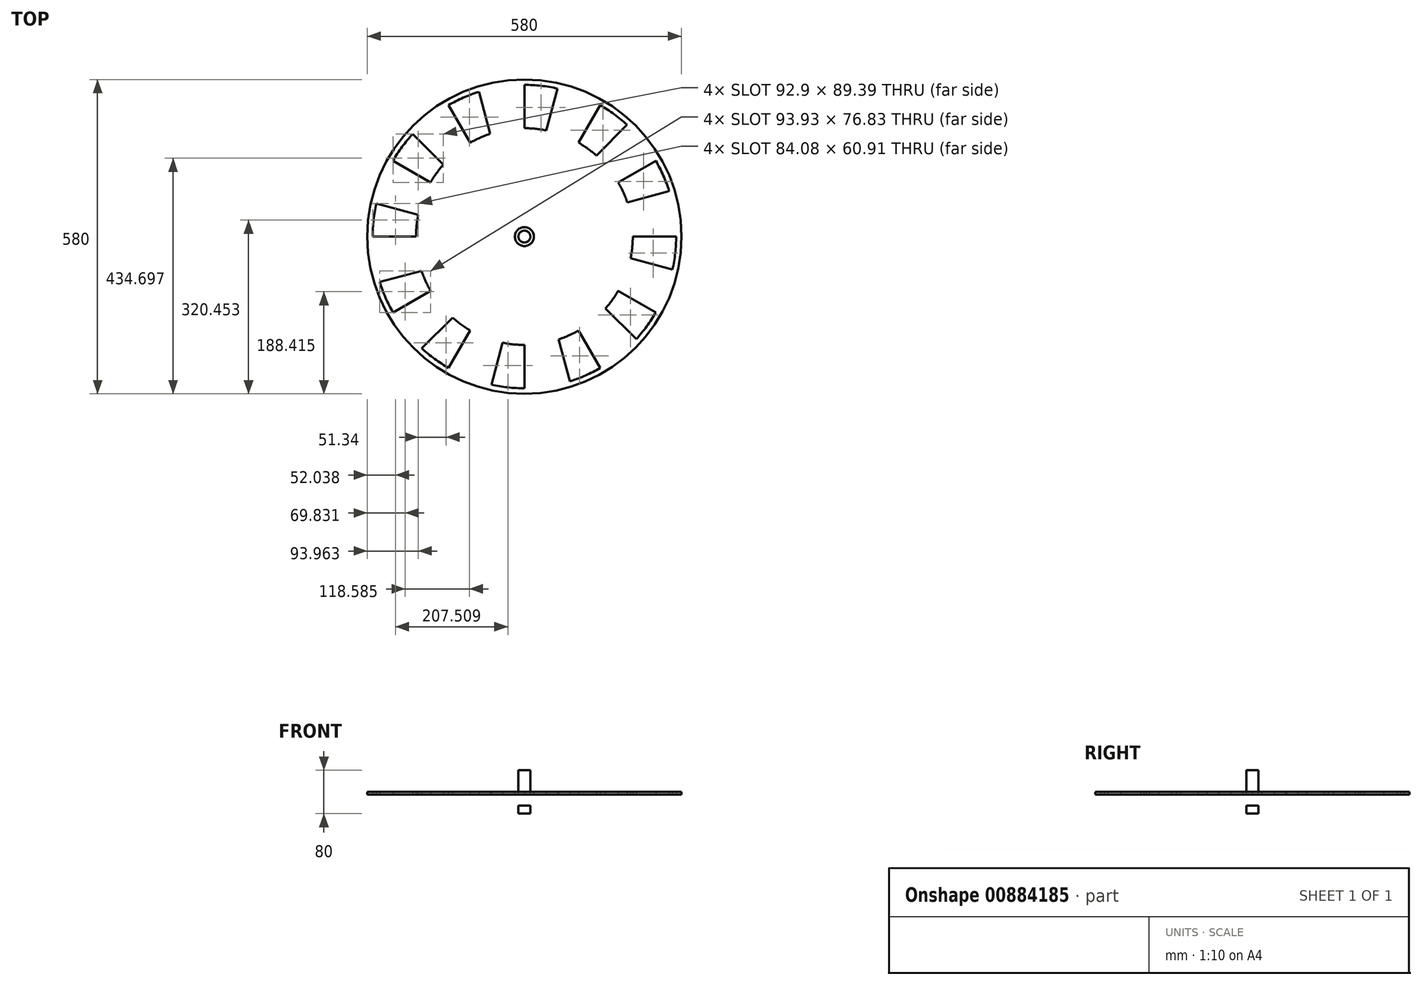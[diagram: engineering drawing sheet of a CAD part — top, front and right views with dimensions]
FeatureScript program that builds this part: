
annotation { "Feature Type Name" : "Feature", "Feature Type Description" : "" }
export const myFeature = defineFeature(function(context is Context, id is Id, definition is map)
    precondition{}
    {
        {
            var Q0;
            Q0=qCreatedBy(makeId("Top.planeOp"),FACE);
            var sketch = newSketch(context, id + "F0", { "sketchPlane" : qUnion([Q0])});
            skArc(sketch, "E0", {"start": v(9.54, 136.41) * mm, "mid": v(4.77, 136.66) * mm, "end": v(0, 136.75) * mm});
            skArc(sketch, "E1", {"start": v(8, 114.55) * mm, "mid": v(4, 114.76) * mm, "end": v(0, 114.83) * mm});
            skLineSegment(sketch, "E2", {"start": v(0, 0) * mm, "end": v(0, 38.61) * mm, "construction": true});
            skLineSegment(sketch, "E3", {"start": v(0, 10) * mm, "end": v(0, 0) * mm, "construction": true});
            skLineSegment(sketch, "E4", {"start": v(0, 0) * mm, "end": v(-47.77, 0) * mm, "construction": true});
            skLineSegment(sketch, "E5", {"start": v(0, 114.83) * mm, "end": v(0, 136.75) * mm});
            skLineSegment(sketch, "E6", {"start": v(8, 114.55) * mm, "end": v(9.54, 136.41) * mm});
            skArc(sketch, "E7.1.0", {"start": v(-10, 114.4) * mm, "mid": v(-14, 113.98) * mm, "end": v(-17.96, 113.42) * mm});
            skLineSegment(sketch, "E7.1.1", {"start": v(-17.96, 113.42) * mm, "end": v(-21.4, 135.06) * mm});
            skArc(sketch, "E7.1.2", {"start": v(-11.92, 136.23) * mm, "mid": v(-16.67, 135.73) * mm, "end": v(-21.4, 135.06) * mm});
            skLineSegment(sketch, "E7.1.3", {"start": v(-10, 114.4) * mm, "end": v(-11.92, 136.23) * mm});
            skArc(sketch, "E7.2.0", {"start": v(-27.78, 111.42) * mm, "mid": v(-31.65, 110.39) * mm, "end": v(-35.49, 109.21) * mm});
            skLineSegment(sketch, "E7.2.1", {"start": v(-35.49, 109.21) * mm, "end": v(-42.26, 130.05) * mm});
            skArc(sketch, "E7.2.2", {"start": v(-33.08, 132.68) * mm, "mid": v(-37.7, 131.45) * mm, "end": v(-42.26, 130.05) * mm});
            skLineSegment(sketch, "E7.2.3", {"start": v(-27.78, 111.42) * mm, "end": v(-33.08, 132.68) * mm});
            skArc(sketch, "E7.3.0", {"start": v(-44.87, 105.7) * mm, "mid": v(-48.53, 104.07) * mm, "end": v(-52.13, 102.32) * mm});
            skLineSegment(sketch, "E7.3.1", {"start": v(-52.13, 102.32) * mm, "end": v(-62.08, 121.84) * mm});
            skArc(sketch, "E7.3.2", {"start": v(-53.43, 125.88) * mm, "mid": v(-57.8, 123.93) * mm, "end": v(-62.08, 121.84) * mm});
            skLineSegment(sketch, "E7.3.3", {"start": v(-44.87, 105.7) * mm, "end": v(-53.43, 125.88) * mm});
            skArc(sketch, "E7.4.0", {"start": v(-60.85, 97.38) * mm, "mid": v(-64.21, 95.2) * mm, "end": v(-67.5, 92.9) * mm});
            skLineSegment(sketch, "E7.4.1", {"start": v(-67.5, 92.9) * mm, "end": v(-80.38, 110.63) * mm});
            skArc(sketch, "E7.4.2", {"start": v(-72.47, 115.97) * mm, "mid": v(-76.47, 113.37) * mm, "end": v(-80.38, 110.63) * mm});
            skLineSegment(sketch, "E7.4.3", {"start": v(-60.85, 97.38) * mm, "end": v(-72.47, 115.97) * mm});
            skArc(sketch, "E7.5.0", {"start": v(-75.34, 86.67) * mm, "mid": v(-78.32, 83.98) * mm, "end": v(-81.2, 81.2) * mm});
            skLineSegment(sketch, "E7.5.1", {"start": v(-81.2, 81.2) * mm, "end": v(-96.7, 96.7) * mm});
            skArc(sketch, "E7.5.2", {"start": v(-89.71, 103.2) * mm, "mid": v(-93.26, 100.01) * mm, "end": v(-96.7, 96.7) * mm});
            skLineSegment(sketch, "E7.5.3", {"start": v(-75.34, 86.67) * mm, "end": v(-89.71, 103.2) * mm});
            skArc(sketch, "E7.6.0", {"start": v(-87.97, 73.81) * mm, "mid": v(-90.5, 70.7) * mm, "end": v(-92.9, 67.5) * mm});
            skLineSegment(sketch, "E7.6.1", {"start": v(-92.9, 67.5) * mm, "end": v(-110.63, 80.38) * mm});
            skArc(sketch, "E7.6.2", {"start": v(-104.75, 87.9) * mm, "mid": v(-107.76, 84.19) * mm, "end": v(-110.63, 80.38) * mm});
            skLineSegment(sketch, "E7.6.3", {"start": v(-87.97, 73.81) * mm, "end": v(-104.75, 87.9) * mm});
            skArc(sketch, "E7.7.0", {"start": v(-98.43, 59.14) * mm, "mid": v(-100.44, 55.67) * mm, "end": v(-102.32, 52.13) * mm});
            skLineSegment(sketch, "E7.7.1", {"start": v(-102.32, 52.13) * mm, "end": v(-121.84, 62.08) * mm});
            skArc(sketch, "E7.7.2", {"start": v(-117.22, 70.43) * mm, "mid": v(-119.6, 66.3) * mm, "end": v(-121.84, 62.08) * mm});
            skLineSegment(sketch, "E7.7.3", {"start": v(-98.43, 59.14) * mm, "end": v(-117.22, 70.43) * mm});
            skArc(sketch, "E7.8.0", {"start": v(-106.47, 43.02) * mm, "mid": v(-107.9, 39.28) * mm, "end": v(-109.21, 35.49) * mm});
            skLineSegment(sketch, "E7.8.1", {"start": v(-109.21, 35.49) * mm, "end": v(-130.05, 42.26) * mm});
            skArc(sketch, "E7.8.2", {"start": v(-126.79, 51.23) * mm, "mid": v(-128.5, 46.77) * mm, "end": v(-130.05, 42.26) * mm});
            skLineSegment(sketch, "E7.8.3", {"start": v(-106.47, 43.02) * mm, "end": v(-126.79, 51.23) * mm});
            skArc(sketch, "E7.9.0", {"start": v(-111.9, 25.83) * mm, "mid": v(-112.72, 21.91) * mm, "end": v(-113.42, 17.96) * mm});
            skLineSegment(sketch, "E7.9.1", {"start": v(-113.42, 17.96) * mm, "end": v(-135.06, 21.4) * mm});
            skArc(sketch, "E7.9.2", {"start": v(-133.24, 30.76) * mm, "mid": v(-134.23, 26.1) * mm, "end": v(-135.06, 21.4) * mm});
            skLineSegment(sketch, "E7.9.3", {"start": v(-111.9, 25.83) * mm, "end": v(-133.24, 30.76) * mm});
            skArc(sketch, "E7.10.0", {"start": v(-114.55, 8) * mm, "mid": v(-114.76, 4) * mm, "end": v(-114.83, 0) * mm});
            skLineSegment(sketch, "E7.10.1", {"start": v(-114.83, 0) * mm, "end": v(-136.75, 0) * mm});
            skArc(sketch, "E7.10.2", {"start": v(-136.41, 9.54) * mm, "mid": v(-136.66, 4.77) * mm, "end": v(-136.75, 0) * mm});
            skLineSegment(sketch, "E7.10.3", {"start": v(-114.55, 8) * mm, "end": v(-136.41, 9.54) * mm});
            skArc(sketch, "E7.11.0", {"start": v(-114.4, -10) * mm, "mid": v(-113.98, -14) * mm, "end": v(-113.42, -17.96) * mm});
            skLineSegment(sketch, "E7.11.1", {"start": v(-113.42, -17.96) * mm, "end": v(-135.06, -21.4) * mm});
            skArc(sketch, "E7.11.2", {"start": v(-136.23, -11.92) * mm, "mid": v(-135.73, -16.67) * mm, "end": v(-135.06, -21.4) * mm});
            skLineSegment(sketch, "E7.11.3", {"start": v(-114.4, -10) * mm, "end": v(-136.23, -11.92) * mm});
            skArc(sketch, "E7.12.0", {"start": v(-111.42, -27.78) * mm, "mid": v(-110.39, -31.65) * mm, "end": v(-109.21, -35.49) * mm});
            skLineSegment(sketch, "E7.12.1", {"start": v(-109.21, -35.49) * mm, "end": v(-130.05, -42.26) * mm});
            skArc(sketch, "E7.12.2", {"start": v(-132.68, -33.08) * mm, "mid": v(-131.45, -37.7) * mm, "end": v(-130.05, -42.26) * mm});
            skLineSegment(sketch, "E7.12.3", {"start": v(-111.42, -27.78) * mm, "end": v(-132.68, -33.08) * mm});
            skArc(sketch, "E7.13.0", {"start": v(-105.7, -44.87) * mm, "mid": v(-104.07, -48.53) * mm, "end": v(-102.32, -52.13) * mm});
            skLineSegment(sketch, "E7.13.1", {"start": v(-102.32, -52.13) * mm, "end": v(-121.84, -62.08) * mm});
            skArc(sketch, "E7.13.2", {"start": v(-125.88, -53.43) * mm, "mid": v(-123.93, -57.8) * mm, "end": v(-121.84, -62.08) * mm});
            skLineSegment(sketch, "E7.13.3", {"start": v(-105.7, -44.87) * mm, "end": v(-125.88, -53.43) * mm});
            skArc(sketch, "E7.14.0", {"start": v(-97.38, -60.85) * mm, "mid": v(-95.2, -64.21) * mm, "end": v(-92.9, -67.5) * mm});
            skLineSegment(sketch, "E7.14.1", {"start": v(-92.9, -67.5) * mm, "end": v(-110.63, -80.38) * mm});
            skArc(sketch, "E7.14.2", {"start": v(-115.97, -72.47) * mm, "mid": v(-113.37, -76.47) * mm, "end": v(-110.63, -80.38) * mm});
            skLineSegment(sketch, "E7.14.3", {"start": v(-97.38, -60.85) * mm, "end": v(-115.97, -72.47) * mm});
            skArc(sketch, "E7.15.0", {"start": v(-86.67, -75.34) * mm, "mid": v(-83.98, -78.32) * mm, "end": v(-81.2, -81.2) * mm});
            skLineSegment(sketch, "E7.15.1", {"start": v(-81.2, -81.2) * mm, "end": v(-96.7, -96.7) * mm});
            skArc(sketch, "E7.15.2", {"start": v(-103.2, -89.71) * mm, "mid": v(-100.01, -93.26) * mm, "end": v(-96.7, -96.7) * mm});
            skLineSegment(sketch, "E7.15.3", {"start": v(-86.67, -75.34) * mm, "end": v(-103.2, -89.71) * mm});
            skArc(sketch, "E7.16.0", {"start": v(-73.81, -87.97) * mm, "mid": v(-70.7, -90.5) * mm, "end": v(-67.5, -92.9) * mm});
            skLineSegment(sketch, "E7.16.1", {"start": v(-67.5, -92.9) * mm, "end": v(-80.38, -110.63) * mm});
            skArc(sketch, "E7.16.2", {"start": v(-87.9, -104.75) * mm, "mid": v(-84.19, -107.76) * mm, "end": v(-80.38, -110.63) * mm});
            skLineSegment(sketch, "E7.16.3", {"start": v(-73.81, -87.97) * mm, "end": v(-87.9, -104.75) * mm});
            skArc(sketch, "E7.17.0", {"start": v(-59.14, -98.43) * mm, "mid": v(-55.67, -100.44) * mm, "end": v(-52.13, -102.32) * mm});
            skLineSegment(sketch, "E7.17.1", {"start": v(-52.13, -102.32) * mm, "end": v(-62.08, -121.84) * mm});
            skArc(sketch, "E7.17.2", {"start": v(-70.43, -117.22) * mm, "mid": v(-66.3, -119.6) * mm, "end": v(-62.08, -121.84) * mm});
            skLineSegment(sketch, "E7.17.3", {"start": v(-59.14, -98.43) * mm, "end": v(-70.43, -117.22) * mm});
            skArc(sketch, "E7.18.0", {"start": v(-43.02, -106.47) * mm, "mid": v(-39.28, -107.9) * mm, "end": v(-35.49, -109.21) * mm});
            skLineSegment(sketch, "E7.18.1", {"start": v(-35.49, -109.21) * mm, "end": v(-42.26, -130.05) * mm});
            skArc(sketch, "E7.18.2", {"start": v(-51.23, -126.79) * mm, "mid": v(-46.77, -128.5) * mm, "end": v(-42.26, -130.05) * mm});
            skLineSegment(sketch, "E7.18.3", {"start": v(-43.02, -106.47) * mm, "end": v(-51.23, -126.79) * mm});
            skArc(sketch, "E7.19.0", {"start": v(-25.83, -111.9) * mm, "mid": v(-21.91, -112.72) * mm, "end": v(-17.96, -113.42) * mm});
            skLineSegment(sketch, "E7.19.1", {"start": v(-17.96, -113.42) * mm, "end": v(-21.4, -135.06) * mm});
            skArc(sketch, "E7.19.2", {"start": v(-30.76, -133.24) * mm, "mid": v(-26.1, -134.23) * mm, "end": v(-21.4, -135.06) * mm});
            skLineSegment(sketch, "E7.19.3", {"start": v(-25.83, -111.9) * mm, "end": v(-30.76, -133.24) * mm});
            skArc(sketch, "E7.20.0", {"start": v(-8, -114.55) * mm, "mid": v(-4, -114.76) * mm, "end": v(0, -114.83) * mm});
            skLineSegment(sketch, "E7.20.1", {"start": v(0, -114.83) * mm, "end": v(0, -136.75) * mm});
            skArc(sketch, "E7.20.2", {"start": v(-9.54, -136.41) * mm, "mid": v(-4.77, -136.66) * mm, "end": v(0, -136.75) * mm});
            skLineSegment(sketch, "E7.20.3", {"start": v(-8, -114.55) * mm, "end": v(-9.54, -136.41) * mm});
            skArc(sketch, "E7.21.0", {"start": v(10, -114.4) * mm, "mid": v(14, -113.98) * mm, "end": v(17.96, -113.42) * mm});
            skLineSegment(sketch, "E7.21.1", {"start": v(17.96, -113.42) * mm, "end": v(21.4, -135.06) * mm});
            skArc(sketch, "E7.21.2", {"start": v(11.92, -136.23) * mm, "mid": v(16.67, -135.73) * mm, "end": v(21.4, -135.06) * mm});
            skLineSegment(sketch, "E7.21.3", {"start": v(10, -114.4) * mm, "end": v(11.92, -136.23) * mm});
            skArc(sketch, "E7.22.0", {"start": v(27.78, -111.42) * mm, "mid": v(31.65, -110.39) * mm, "end": v(35.49, -109.21) * mm});
            skLineSegment(sketch, "E7.22.1", {"start": v(35.49, -109.21) * mm, "end": v(42.26, -130.05) * mm});
            skArc(sketch, "E7.22.2", {"start": v(33.08, -132.68) * mm, "mid": v(37.7, -131.45) * mm, "end": v(42.26, -130.05) * mm});
            skLineSegment(sketch, "E7.22.3", {"start": v(27.78, -111.42) * mm, "end": v(33.08, -132.68) * mm});
            skArc(sketch, "E7.23.0", {"start": v(44.87, -105.7) * mm, "mid": v(48.53, -104.07) * mm, "end": v(52.13, -102.32) * mm});
            skLineSegment(sketch, "E7.23.1", {"start": v(52.13, -102.32) * mm, "end": v(62.08, -121.84) * mm});
            skArc(sketch, "E7.23.2", {"start": v(53.43, -125.88) * mm, "mid": v(57.8, -123.93) * mm, "end": v(62.08, -121.84) * mm});
            skLineSegment(sketch, "E7.23.3", {"start": v(44.87, -105.7) * mm, "end": v(53.43, -125.88) * mm});
            skArc(sketch, "E7.24.0", {"start": v(60.85, -97.38) * mm, "mid": v(64.21, -95.2) * mm, "end": v(67.5, -92.9) * mm});
            skLineSegment(sketch, "E7.24.1", {"start": v(67.5, -92.9) * mm, "end": v(80.38, -110.63) * mm});
            skArc(sketch, "E7.24.2", {"start": v(72.47, -115.97) * mm, "mid": v(76.47, -113.37) * mm, "end": v(80.38, -110.63) * mm});
            skLineSegment(sketch, "E7.24.3", {"start": v(60.85, -97.38) * mm, "end": v(72.47, -115.97) * mm});
            skArc(sketch, "E7.25.0", {"start": v(75.34, -86.67) * mm, "mid": v(78.32, -83.98) * mm, "end": v(81.2, -81.2) * mm});
            skLineSegment(sketch, "E7.25.1", {"start": v(81.2, -81.2) * mm, "end": v(96.7, -96.7) * mm});
            skArc(sketch, "E7.25.2", {"start": v(89.71, -103.2) * mm, "mid": v(93.26, -100.01) * mm, "end": v(96.7, -96.7) * mm});
            skLineSegment(sketch, "E7.25.3", {"start": v(75.34, -86.67) * mm, "end": v(89.71, -103.2) * mm});
            skArc(sketch, "E7.26.0", {"start": v(87.97, -73.81) * mm, "mid": v(90.5, -70.7) * mm, "end": v(92.9, -67.5) * mm});
            skLineSegment(sketch, "E7.26.1", {"start": v(92.9, -67.5) * mm, "end": v(110.63, -80.38) * mm});
            skArc(sketch, "E7.26.2", {"start": v(104.75, -87.9) * mm, "mid": v(107.76, -84.19) * mm, "end": v(110.63, -80.38) * mm});
            skLineSegment(sketch, "E7.26.3", {"start": v(87.97, -73.81) * mm, "end": v(104.75, -87.9) * mm});
            skArc(sketch, "E7.27.0", {"start": v(98.43, -59.14) * mm, "mid": v(100.44, -55.67) * mm, "end": v(102.32, -52.13) * mm});
            skLineSegment(sketch, "E7.27.1", {"start": v(102.32, -52.13) * mm, "end": v(121.84, -62.08) * mm});
            skArc(sketch, "E7.27.2", {"start": v(117.22, -70.43) * mm, "mid": v(119.6, -66.3) * mm, "end": v(121.84, -62.08) * mm});
            skLineSegment(sketch, "E7.27.3", {"start": v(98.43, -59.14) * mm, "end": v(117.22, -70.43) * mm});
            skArc(sketch, "E7.28.0", {"start": v(106.47, -43.02) * mm, "mid": v(107.9, -39.28) * mm, "end": v(109.21, -35.49) * mm});
            skLineSegment(sketch, "E7.28.1", {"start": v(109.21, -35.49) * mm, "end": v(130.05, -42.26) * mm});
            skArc(sketch, "E7.28.2", {"start": v(126.79, -51.23) * mm, "mid": v(128.5, -46.77) * mm, "end": v(130.05, -42.26) * mm});
            skLineSegment(sketch, "E7.28.3", {"start": v(106.47, -43.02) * mm, "end": v(126.79, -51.23) * mm});
            skArc(sketch, "E7.29.0", {"start": v(111.9, -25.83) * mm, "mid": v(112.72, -21.91) * mm, "end": v(113.42, -17.96) * mm});
            skLineSegment(sketch, "E7.29.1", {"start": v(113.42, -17.96) * mm, "end": v(135.06, -21.4) * mm});
            skArc(sketch, "E7.29.2", {"start": v(133.24, -30.76) * mm, "mid": v(134.23, -26.1) * mm, "end": v(135.06, -21.4) * mm});
            skLineSegment(sketch, "E7.29.3", {"start": v(111.9, -25.83) * mm, "end": v(133.24, -30.76) * mm});
            skArc(sketch, "E7.30.0", {"start": v(114.55, -8) * mm, "mid": v(114.76, -4) * mm, "end": v(114.83, 0) * mm});
            skLineSegment(sketch, "E7.30.1", {"start": v(114.83, 0) * mm, "end": v(136.75, 0) * mm});
            skArc(sketch, "E7.30.2", {"start": v(136.41, -9.54) * mm, "mid": v(136.66, -4.77) * mm, "end": v(136.75, 0) * mm});
            skLineSegment(sketch, "E7.30.3", {"start": v(114.55, -8) * mm, "end": v(136.41, -9.54) * mm});
            skArc(sketch, "E7.31.0", {"start": v(114.4, 10) * mm, "mid": v(113.98, 14) * mm, "end": v(113.42, 17.96) * mm});
            skLineSegment(sketch, "E7.31.1", {"start": v(113.42, 17.96) * mm, "end": v(135.06, 21.4) * mm});
            skArc(sketch, "E7.31.2", {"start": v(136.23, 11.92) * mm, "mid": v(135.73, 16.67) * mm, "end": v(135.06, 21.4) * mm});
            skLineSegment(sketch, "E7.31.3", {"start": v(114.4, 10) * mm, "end": v(136.23, 11.92) * mm});
            skArc(sketch, "E7.32.0", {"start": v(111.42, 27.78) * mm, "mid": v(110.39, 31.65) * mm, "end": v(109.21, 35.49) * mm});
            skLineSegment(sketch, "E7.32.1", {"start": v(109.21, 35.49) * mm, "end": v(130.05, 42.26) * mm});
            skArc(sketch, "E7.32.2", {"start": v(132.68, 33.08) * mm, "mid": v(131.45, 37.7) * mm, "end": v(130.05, 42.26) * mm});
            skLineSegment(sketch, "E7.32.3", {"start": v(111.42, 27.78) * mm, "end": v(132.68, 33.08) * mm});
            skArc(sketch, "E7.33.0", {"start": v(105.7, 44.87) * mm, "mid": v(104.07, 48.53) * mm, "end": v(102.32, 52.13) * mm});
            skLineSegment(sketch, "E7.33.1", {"start": v(102.32, 52.13) * mm, "end": v(121.84, 62.08) * mm});
            skArc(sketch, "E7.33.2", {"start": v(125.88, 53.43) * mm, "mid": v(123.93, 57.8) * mm, "end": v(121.84, 62.08) * mm});
            skLineSegment(sketch, "E7.33.3", {"start": v(105.7, 44.87) * mm, "end": v(125.88, 53.43) * mm});
            skArc(sketch, "E7.34.0", {"start": v(97.38, 60.85) * mm, "mid": v(95.2, 64.21) * mm, "end": v(92.9, 67.5) * mm});
            skLineSegment(sketch, "E7.34.1", {"start": v(92.9, 67.5) * mm, "end": v(110.63, 80.38) * mm});
            skArc(sketch, "E7.34.2", {"start": v(115.97, 72.47) * mm, "mid": v(113.37, 76.47) * mm, "end": v(110.63, 80.38) * mm});
            skLineSegment(sketch, "E7.34.3", {"start": v(97.38, 60.85) * mm, "end": v(115.97, 72.47) * mm});
            skArc(sketch, "E7.35.0", {"start": v(86.67, 75.34) * mm, "mid": v(83.98, 78.32) * mm, "end": v(81.2, 81.2) * mm});
            skLineSegment(sketch, "E7.35.1", {"start": v(81.2, 81.2) * mm, "end": v(96.7, 96.7) * mm});
            skArc(sketch, "E7.35.2", {"start": v(103.2, 89.71) * mm, "mid": v(100.01, 93.26) * mm, "end": v(96.7, 96.7) * mm});
            skLineSegment(sketch, "E7.35.3", {"start": v(86.67, 75.34) * mm, "end": v(103.2, 89.71) * mm});
            skArc(sketch, "E7.36.0", {"start": v(73.81, 87.97) * mm, "mid": v(70.7, 90.5) * mm, "end": v(67.5, 92.9) * mm});
            skLineSegment(sketch, "E7.36.1", {"start": v(67.5, 92.9) * mm, "end": v(80.38, 110.63) * mm});
            skArc(sketch, "E7.36.2", {"start": v(87.9, 104.75) * mm, "mid": v(84.19, 107.76) * mm, "end": v(80.38, 110.63) * mm});
            skLineSegment(sketch, "E7.36.3", {"start": v(73.81, 87.97) * mm, "end": v(87.9, 104.75) * mm});
            skArc(sketch, "E7.37.0", {"start": v(59.14, 98.43) * mm, "mid": v(55.67, 100.44) * mm, "end": v(52.13, 102.32) * mm});
            skLineSegment(sketch, "E7.37.1", {"start": v(52.13, 102.32) * mm, "end": v(62.08, 121.84) * mm});
            skArc(sketch, "E7.37.2", {"start": v(70.43, 117.22) * mm, "mid": v(66.3, 119.6) * mm, "end": v(62.08, 121.84) * mm});
            skLineSegment(sketch, "E7.37.3", {"start": v(59.14, 98.43) * mm, "end": v(70.43, 117.22) * mm});
            skArc(sketch, "E7.38.0", {"start": v(43.02, 106.47) * mm, "mid": v(39.28, 107.9) * mm, "end": v(35.49, 109.21) * mm});
            skLineSegment(sketch, "E7.38.1", {"start": v(35.49, 109.21) * mm, "end": v(42.26, 130.05) * mm});
            skArc(sketch, "E7.38.2", {"start": v(51.23, 126.79) * mm, "mid": v(46.77, 128.5) * mm, "end": v(42.26, 130.05) * mm});
            skLineSegment(sketch, "E7.38.3", {"start": v(43.02, 106.47) * mm, "end": v(51.23, 126.79) * mm});
            skArc(sketch, "E7.39.0", {"start": v(25.83, 111.9) * mm, "mid": v(21.91, 112.72) * mm, "end": v(17.96, 113.42) * mm});
            skLineSegment(sketch, "E7.39.1", {"start": v(17.96, 113.42) * mm, "end": v(21.4, 135.06) * mm});
            skArc(sketch, "E7.39.2", {"start": v(30.76, 133.24) * mm, "mid": v(26.1, 134.23) * mm, "end": v(21.4, 135.06) * mm});
            skLineSegment(sketch, "E7.39.3", {"start": v(25.83, 111.9) * mm, "end": v(30.76, 133.24) * mm});
            skCircle(sketch, "E8", {"center": v(0, 0) * mm, "radius": 290 * mm});
            skArc(sketch, "E9", {"start": v(40.17, 195.92) * mm, "mid": v(20.2, 198.98) * mm, "end": v(0, 200) * mm});
            skArc(sketch, "E10", {"start": v(60.9, 273.3) * mm, "mid": v(30.64, 278.32) * mm, "end": v(0, 280) * mm});
            skLineSegment(sketch, "E11", {"start": v(0, 0) * mm, "end": v(0, 38.61) * mm});
            skLineSegment(sketch, "E12.trimOffspring", {"start": v(0, 200) * mm, "end": v(0, 280) * mm});
            skLineSegment(sketch, "E13.trimOffspring", {"start": v(40.17, 195.92) * mm, "end": v(60.9, 273.3) * mm});
            skLineSegment(sketch, "E14.trimOffspring", {"start": v(0, 114.83) * mm, "end": v(0, 145) * mm});
            skArc(sketch, "E15.1.0", {"start": v(-63.17, 189.76) * mm, "mid": v(-82, 182.42) * mm, "end": v(-100, 173.2) * mm});
            skLineSegment(sketch, "E15.1.1", {"start": v(-100, 173.2) * mm, "end": v(-140, 242.49) * mm});
            skArc(sketch, "E15.1.2", {"start": v(-83.9, 267.13) * mm, "mid": v(-112.63, 256.35) * mm, "end": v(-140, 242.49) * mm});
            skLineSegment(sketch, "E15.1.3", {"start": v(-63.17, 189.76) * mm, "end": v(-83.9, 267.13) * mm});
            skArc(sketch, "E15.2.0", {"start": v(-149.59, 132.75) * mm, "mid": v(-162.23, 116.97) * mm, "end": v(-173.2, 100) * mm});
            skLineSegment(sketch, "E15.2.1", {"start": v(-173.2, 100) * mm, "end": v(-242.49, 140) * mm});
            skArc(sketch, "E15.2.2", {"start": v(-206.23, 189.4) * mm, "mid": v(-225.71, 165.7) * mm, "end": v(-242.49, 140) * mm});
            skLineSegment(sketch, "E15.2.3", {"start": v(-149.59, 132.75) * mm, "end": v(-206.23, 189.4) * mm});
            skArc(sketch, "E15.3.0", {"start": v(-195.92, 40.17) * mm, "mid": v(-198.98, 20.2) * mm, "end": v(-200, 0) * mm});
            skLineSegment(sketch, "E15.3.1", {"start": v(-200, 0) * mm, "end": v(-280, 0) * mm});
            skArc(sketch, "E15.3.2", {"start": v(-273.3, 60.9) * mm, "mid": v(-278.32, 30.64) * mm, "end": v(-280, 0) * mm});
            skLineSegment(sketch, "E15.3.3", {"start": v(-195.92, 40.17) * mm, "end": v(-273.3, 60.9) * mm});
            skArc(sketch, "E15.4.0", {"start": v(-189.76, -63.17) * mm, "mid": v(-182.42, -82) * mm, "end": v(-173.2, -100) * mm});
            skLineSegment(sketch, "E15.4.1", {"start": v(-173.2, -100) * mm, "end": v(-242.49, -140) * mm});
            skArc(sketch, "E15.4.2", {"start": v(-267.13, -83.9) * mm, "mid": v(-256.35, -112.63) * mm, "end": v(-242.49, -140) * mm});
            skLineSegment(sketch, "E15.4.3", {"start": v(-189.76, -63.17) * mm, "end": v(-267.13, -83.9) * mm});
            skArc(sketch, "E15.5.0", {"start": v(-132.75, -149.59) * mm, "mid": v(-116.97, -162.23) * mm, "end": v(-100, -173.2) * mm});
            skLineSegment(sketch, "E15.5.1", {"start": v(-100, -173.2) * mm, "end": v(-140, -242.49) * mm});
            skArc(sketch, "E15.5.2", {"start": v(-189.4, -206.23) * mm, "mid": v(-165.7, -225.71) * mm, "end": v(-140, -242.49) * mm});
            skLineSegment(sketch, "E15.5.3", {"start": v(-132.75, -149.59) * mm, "end": v(-189.4, -206.23) * mm});
            skArc(sketch, "E15.6.0", {"start": v(-40.17, -195.92) * mm, "mid": v(-20.2, -198.98) * mm, "end": v(0, -200) * mm});
            skLineSegment(sketch, "E15.6.1", {"start": v(0, -200) * mm, "end": v(0, -280) * mm});
            skArc(sketch, "E15.6.2", {"start": v(-60.9, -273.3) * mm, "mid": v(-30.64, -278.32) * mm, "end": v(0, -280) * mm});
            skLineSegment(sketch, "E15.6.3", {"start": v(-40.17, -195.92) * mm, "end": v(-60.9, -273.3) * mm});
            skArc(sketch, "E15.7.0", {"start": v(63.17, -189.76) * mm, "mid": v(82, -182.42) * mm, "end": v(100, -173.2) * mm});
            skLineSegment(sketch, "E15.7.1", {"start": v(100, -173.2) * mm, "end": v(140, -242.49) * mm});
            skArc(sketch, "E15.7.2", {"start": v(83.9, -267.13) * mm, "mid": v(112.63, -256.35) * mm, "end": v(140, -242.49) * mm});
            skLineSegment(sketch, "E15.7.3", {"start": v(63.17, -189.76) * mm, "end": v(83.9, -267.13) * mm});
            skArc(sketch, "E15.8.0", {"start": v(149.59, -132.75) * mm, "mid": v(162.23, -116.97) * mm, "end": v(173.2, -100) * mm});
            skLineSegment(sketch, "E15.8.1", {"start": v(173.2, -100) * mm, "end": v(242.49, -140) * mm});
            skArc(sketch, "E15.8.2", {"start": v(206.23, -189.4) * mm, "mid": v(225.71, -165.7) * mm, "end": v(242.49, -140) * mm});
            skLineSegment(sketch, "E15.8.3", {"start": v(149.59, -132.75) * mm, "end": v(206.23, -189.4) * mm});
            skArc(sketch, "E15.9.0", {"start": v(195.92, -40.17) * mm, "mid": v(198.98, -20.2) * mm, "end": v(200, 0) * mm});
            skLineSegment(sketch, "E15.9.1", {"start": v(200, 0) * mm, "end": v(280, 0) * mm});
            skArc(sketch, "E15.9.2", {"start": v(273.3, -60.9) * mm, "mid": v(278.32, -30.64) * mm, "end": v(280, 0) * mm});
            skLineSegment(sketch, "E15.9.3", {"start": v(195.92, -40.17) * mm, "end": v(273.3, -60.9) * mm});
            skArc(sketch, "E15.10.0", {"start": v(189.76, 63.17) * mm, "mid": v(182.42, 82) * mm, "end": v(173.2, 100) * mm});
            skLineSegment(sketch, "E15.10.1", {"start": v(173.2, 100) * mm, "end": v(242.49, 140) * mm});
            skArc(sketch, "E15.10.2", {"start": v(267.13, 83.9) * mm, "mid": v(256.35, 112.63) * mm, "end": v(242.49, 140) * mm});
            skLineSegment(sketch, "E15.10.3", {"start": v(189.76, 63.17) * mm, "end": v(267.13, 83.9) * mm});
            skArc(sketch, "E15.11.0", {"start": v(132.75, 149.59) * mm, "mid": v(116.97, 162.23) * mm, "end": v(100, 173.2) * mm});
            skLineSegment(sketch, "E15.11.1", {"start": v(100, 173.2) * mm, "end": v(140, 242.49) * mm});
            skArc(sketch, "E15.11.2", {"start": v(189.4, 206.23) * mm, "mid": v(165.7, 225.71) * mm, "end": v(140, 242.49) * mm});
            skLineSegment(sketch, "E15.11.3", {"start": v(132.75, 149.59) * mm, "end": v(189.4, 206.23) * mm});
            skLineSegment(sketch, "E16.bottom", {"start": v(5, -5) * mm, "end": v(-5, -5) * mm});
            skLineSegment(sketch, "E16.top", {"start": v(5, 5) * mm, "end": v(-5, 5) * mm});
            skLineSegment(sketch, "E16.left", {"start": v(5, -5) * mm, "end": v(5, 5) * mm});
            skLineSegment(sketch, "E16.right", {"start": v(-5, -5) * mm, "end": v(-5, 5) * mm});
            skSolve(sketch);
        }
        {
            var Q0;
            Q0=qSketchRegion(id+"F0",true);
            extrude(context, id + "F1", {"entities" : qUnion([Q0]), "depth" : 5 * mm, "offsetDistance" : 25 * mm});
        }
        {
            var Q0;
            Q0=makeQuery(id+"F1.opExtrude","CAP_FACE",FACE,{"disambiguationData":[OSD([sQuery(id+"F0.wireOp",EDGE,"E0"),sQuery(id+"F0.wireOp",EDGE,"E1"),sQuery(id+"F0.wireOp",EDGE,"E6"),sQuery(id+"F0.wireOp",EDGE,"E7.1.0"),sQuery(id+"F0.wireOp",EDGE,"E7.1.1"),sQuery(id+"F0.wireOp",EDGE,"E7.1.2"),sQuery(id+"F0.wireOp",EDGE,"E7.1.3"),sQuery(id+"F0.wireOp",EDGE,"E7.2.0"),sQuery(id+"F0.wireOp",EDGE,"E7.2.1"),sQuery(id+"F0.wireOp",EDGE,"E7.2.2"),sQuery(id+"F0.wireOp",EDGE,"E7.2.3"),sQuery(id+"F0.wireOp",EDGE,"E7.3.0"),sQuery(id+"F0.wireOp",EDGE,"E7.3.1"),sQuery(id+"F0.wireOp",EDGE,"E7.3.2"),sQuery(id+"F0.wireOp",EDGE,"E7.3.3"),sQuery(id+"F0.wireOp",EDGE,"E7.4.0"),sQuery(id+"F0.wireOp",EDGE,"E7.4.1"),sQuery(id+"F0.wireOp",EDGE,"E7.4.2"),sQuery(id+"F0.wireOp",EDGE,"E7.4.3"),sQuery(id+"F0.wireOp",EDGE,"E7.5.0"),sQuery(id+"F0.wireOp",EDGE,"E7.5.1"),sQuery(id+"F0.wireOp",EDGE,"E7.5.2"),sQuery(id+"F0.wireOp",EDGE,"E7.5.3"),sQuery(id+"F0.wireOp",EDGE,"E7.6.0"),sQuery(id+"F0.wireOp",EDGE,"E7.6.1"),sQuery(id+"F0.wireOp",EDGE,"E7.6.2"),sQuery(id+"F0.wireOp",EDGE,"E7.6.3"),sQuery(id+"F0.wireOp",EDGE,"E7.7.0"),sQuery(id+"F0.wireOp",EDGE,"E7.7.1"),sQuery(id+"F0.wireOp",EDGE,"E7.7.2"),sQuery(id+"F0.wireOp",EDGE,"E7.7.3"),sQuery(id+"F0.wireOp",EDGE,"E7.8.0"),sQuery(id+"F0.wireOp",EDGE,"E7.8.1"),sQuery(id+"F0.wireOp",EDGE,"E7.8.2"),sQuery(id+"F0.wireOp",EDGE,"E7.8.3"),sQuery(id+"F0.wireOp",EDGE,"E7.9.0"),sQuery(id+"F0.wireOp",EDGE,"E7.9.1"),sQuery(id+"F0.wireOp",EDGE,"E7.9.2"),sQuery(id+"F0.wireOp",EDGE,"E7.9.3"),sQuery(id+"F0.wireOp",EDGE,"E7.10.0"),sQuery(id+"F0.wireOp",EDGE,"E7.10.1"),sQuery(id+"F0.wireOp",EDGE,"E7.10.2"),sQuery(id+"F0.wireOp",EDGE,"E7.10.3"),sQuery(id+"F0.wireOp",EDGE,"E7.11.0"),sQuery(id+"F0.wireOp",EDGE,"E7.11.1"),sQuery(id+"F0.wireOp",EDGE,"E7.11.2"),sQuery(id+"F0.wireOp",EDGE,"E7.11.3"),sQuery(id+"F0.wireOp",EDGE,"E7.12.0"),sQuery(id+"F0.wireOp",EDGE,"E7.12.1"),sQuery(id+"F0.wireOp",EDGE,"E7.12.2"),sQuery(id+"F0.wireOp",EDGE,"E7.12.3"),sQuery(id+"F0.wireOp",EDGE,"E7.13.0"),sQuery(id+"F0.wireOp",EDGE,"E7.13.1"),sQuery(id+"F0.wireOp",EDGE,"E7.13.2"),sQuery(id+"F0.wireOp",EDGE,"E7.13.3"),sQuery(id+"F0.wireOp",EDGE,"E7.14.0"),sQuery(id+"F0.wireOp",EDGE,"E7.14.1"),sQuery(id+"F0.wireOp",EDGE,"E7.14.2"),sQuery(id+"F0.wireOp",EDGE,"E7.14.3"),sQuery(id+"F0.wireOp",EDGE,"E7.15.0"),sQuery(id+"F0.wireOp",EDGE,"E7.15.1"),sQuery(id+"F0.wireOp",EDGE,"E7.15.2"),sQuery(id+"F0.wireOp",EDGE,"E7.15.3"),sQuery(id+"F0.wireOp",EDGE,"E7.16.0"),sQuery(id+"F0.wireOp",EDGE,"E7.16.1"),sQuery(id+"F0.wireOp",EDGE,"E7.16.2"),sQuery(id+"F0.wireOp",EDGE,"E7.16.3"),sQuery(id+"F0.wireOp",EDGE,"E7.17.0"),sQuery(id+"F0.wireOp",EDGE,"E7.17.1"),sQuery(id+"F0.wireOp",EDGE,"E7.17.2"),sQuery(id+"F0.wireOp",EDGE,"E7.17.3"),sQuery(id+"F0.wireOp",EDGE,"E7.18.0"),sQuery(id+"F0.wireOp",EDGE,"E7.18.1"),sQuery(id+"F0.wireOp",EDGE,"E7.18.2"),sQuery(id+"F0.wireOp",EDGE,"E7.18.3"),sQuery(id+"F0.wireOp",EDGE,"E7.19.0"),sQuery(id+"F0.wireOp",EDGE,"E7.19.1"),sQuery(id+"F0.wireOp",EDGE,"E7.19.2"),sQuery(id+"F0.wireOp",EDGE,"E7.19.3"),sQuery(id+"F0.wireOp",EDGE,"E7.20.0"),sQuery(id+"F0.wireOp",EDGE,"E7.20.1"),sQuery(id+"F0.wireOp",EDGE,"E7.20.2"),sQuery(id+"F0.wireOp",EDGE,"E7.20.3"),sQuery(id+"F0.wireOp",EDGE,"E7.21.0"),sQuery(id+"F0.wireOp",EDGE,"E7.21.1"),sQuery(id+"F0.wireOp",EDGE,"E7.21.2"),sQuery(id+"F0.wireOp",EDGE,"E7.21.3"),sQuery(id+"F0.wireOp",EDGE,"E7.22.0"),sQuery(id+"F0.wireOp",EDGE,"E7.22.1"),sQuery(id+"F0.wireOp",EDGE,"E7.22.2"),sQuery(id+"F0.wireOp",EDGE,"E7.22.3"),sQuery(id+"F0.wireOp",EDGE,"E7.23.0"),sQuery(id+"F0.wireOp",EDGE,"E7.23.1"),sQuery(id+"F0.wireOp",EDGE,"E7.23.2"),sQuery(id+"F0.wireOp",EDGE,"E7.23.3"),sQuery(id+"F0.wireOp",EDGE,"E7.24.0"),sQuery(id+"F0.wireOp",EDGE,"E7.24.1"),sQuery(id+"F0.wireOp",EDGE,"E7.24.2"),sQuery(id+"F0.wireOp",EDGE,"E7.24.3"),sQuery(id+"F0.wireOp",EDGE,"E7.25.0"),sQuery(id+"F0.wireOp",EDGE,"E7.25.1"),sQuery(id+"F0.wireOp",EDGE,"E7.25.2"),sQuery(id+"F0.wireOp",EDGE,"E7.25.3"),sQuery(id+"F0.wireOp",EDGE,"E7.26.0"),sQuery(id+"F0.wireOp",EDGE,"E7.26.1"),sQuery(id+"F0.wireOp",EDGE,"E7.26.2"),sQuery(id+"F0.wireOp",EDGE,"E7.26.3"),sQuery(id+"F0.wireOp",EDGE,"E7.27.0"),sQuery(id+"F0.wireOp",EDGE,"E7.27.1"),sQuery(id+"F0.wireOp",EDGE,"E7.27.2"),sQuery(id+"F0.wireOp",EDGE,"E7.27.3"),sQuery(id+"F0.wireOp",EDGE,"E7.28.0"),sQuery(id+"F0.wireOp",EDGE,"E7.28.1"),sQuery(id+"F0.wireOp",EDGE,"E7.28.2"),sQuery(id+"F0.wireOp",EDGE,"E7.28.3"),sQuery(id+"F0.wireOp",EDGE,"E7.29.0"),sQuery(id+"F0.wireOp",EDGE,"E7.29.1"),sQuery(id+"F0.wireOp",EDGE,"E7.29.2"),sQuery(id+"F0.wireOp",EDGE,"E7.29.3"),sQuery(id+"F0.wireOp",EDGE,"E7.30.0"),sQuery(id+"F0.wireOp",EDGE,"E7.30.1"),sQuery(id+"F0.wireOp",EDGE,"E7.30.2"),sQuery(id+"F0.wireOp",EDGE,"E7.30.3"),sQuery(id+"F0.wireOp",EDGE,"E7.31.0"),sQuery(id+"F0.wireOp",EDGE,"E7.31.1"),sQuery(id+"F0.wireOp",EDGE,"E7.31.2"),sQuery(id+"F0.wireOp",EDGE,"E7.31.3"),sQuery(id+"F0.wireOp",EDGE,"E7.32.0"),sQuery(id+"F0.wireOp",EDGE,"E7.32.1"),sQuery(id+"F0.wireOp",EDGE,"E7.32.2"),sQuery(id+"F0.wireOp",EDGE,"E7.32.3"),sQuery(id+"F0.wireOp",EDGE,"E7.33.0"),sQuery(id+"F0.wireOp",EDGE,"E7.33.1"),sQuery(id+"F0.wireOp",EDGE,"E7.33.2"),sQuery(id+"F0.wireOp",EDGE,"E7.33.3"),sQuery(id+"F0.wireOp",EDGE,"E7.34.0"),sQuery(id+"F0.wireOp",EDGE,"E7.34.1"),sQuery(id+"F0.wireOp",EDGE,"E7.34.2"),sQuery(id+"F0.wireOp",EDGE,"E7.34.3"),sQuery(id+"F0.wireOp",EDGE,"E7.35.0"),sQuery(id+"F0.wireOp",EDGE,"E7.35.1"),sQuery(id+"F0.wireOp",EDGE,"E7.35.2"),sQuery(id+"F0.wireOp",EDGE,"E7.35.3"),sQuery(id+"F0.wireOp",EDGE,"E7.36.0"),sQuery(id+"F0.wireOp",EDGE,"E7.36.1"),sQuery(id+"F0.wireOp",EDGE,"E7.36.2"),sQuery(id+"F0.wireOp",EDGE,"E7.36.3"),sQuery(id+"F0.wireOp",EDGE,"E7.37.0"),sQuery(id+"F0.wireOp",EDGE,"E7.37.1"),sQuery(id+"F0.wireOp",EDGE,"E7.37.2"),sQuery(id+"F0.wireOp",EDGE,"E7.37.3"),sQuery(id+"F0.wireOp",EDGE,"E7.38.0"),sQuery(id+"F0.wireOp",EDGE,"E7.38.1"),sQuery(id+"F0.wireOp",EDGE,"E7.38.2"),sQuery(id+"F0.wireOp",EDGE,"E7.38.3"),sQuery(id+"F0.wireOp",EDGE,"E7.39.0"),sQuery(id+"F0.wireOp",EDGE,"E7.39.1"),sQuery(id+"F0.wireOp",EDGE,"E7.39.2"),sQuery(id+"F0.wireOp",EDGE,"E7.39.3"),sQuery(id+"F0.wireOp",EDGE,"E8"),sQuery(id+"F0.wireOp",EDGE,"E9"),sQuery(id+"F0.wireOp",EDGE,"E10"),sQuery(id+"F0.wireOp",EDGE,"E12.trimOffspring"),sQuery(id+"F0.wireOp",EDGE,"E13.trimOffspring"),sQuery(id+"F0.wireOp",EDGE,"E14.trimOffspring"),sQuery(id+"F0.wireOp",EDGE,"E15.1.0"),sQuery(id+"F0.wireOp",EDGE,"E15.1.1"),sQuery(id+"F0.wireOp",EDGE,"E15.1.2"),sQuery(id+"F0.wireOp",EDGE,"E15.1.3"),sQuery(id+"F0.wireOp",EDGE,"E15.2.0"),sQuery(id+"F0.wireOp",EDGE,"E15.2.1"),sQuery(id+"F0.wireOp",EDGE,"E15.2.2"),sQuery(id+"F0.wireOp",EDGE,"E15.2.3"),sQuery(id+"F0.wireOp",EDGE,"E15.3.0"),sQuery(id+"F0.wireOp",EDGE,"E15.3.1"),sQuery(id+"F0.wireOp",EDGE,"E15.3.2"),sQuery(id+"F0.wireOp",EDGE,"E15.3.3"),sQuery(id+"F0.wireOp",EDGE,"E15.4.0"),sQuery(id+"F0.wireOp",EDGE,"E15.4.1"),sQuery(id+"F0.wireOp",EDGE,"E15.4.2"),sQuery(id+"F0.wireOp",EDGE,"E15.4.3"),sQuery(id+"F0.wireOp",EDGE,"E15.5.0"),sQuery(id+"F0.wireOp",EDGE,"E15.5.1"),sQuery(id+"F0.wireOp",EDGE,"E15.5.2"),sQuery(id+"F0.wireOp",EDGE,"E15.5.3"),sQuery(id+"F0.wireOp",EDGE,"E15.6.0"),sQuery(id+"F0.wireOp",EDGE,"E15.6.1"),sQuery(id+"F0.wireOp",EDGE,"E15.6.2"),sQuery(id+"F0.wireOp",EDGE,"E15.6.3"),sQuery(id+"F0.wireOp",EDGE,"E15.7.0"),sQuery(id+"F0.wireOp",EDGE,"E15.7.1"),sQuery(id+"F0.wireOp",EDGE,"E15.7.2"),sQuery(id+"F0.wireOp",EDGE,"E15.7.3"),sQuery(id+"F0.wireOp",EDGE,"E15.8.0"),sQuery(id+"F0.wireOp",EDGE,"E15.8.1"),sQuery(id+"F0.wireOp",EDGE,"E15.8.2"),sQuery(id+"F0.wireOp",EDGE,"E15.8.3"),sQuery(id+"F0.wireOp",EDGE,"E15.9.0"),sQuery(id+"F0.wireOp",EDGE,"E15.9.1"),sQuery(id+"F0.wireOp",EDGE,"E15.9.2"),sQuery(id+"F0.wireOp",EDGE,"E15.9.3"),sQuery(id+"F0.wireOp",EDGE,"E15.10.0"),sQuery(id+"F0.wireOp",EDGE,"E15.10.1"),sQuery(id+"F0.wireOp",EDGE,"E15.10.2"),sQuery(id+"F0.wireOp",EDGE,"E15.10.3"),sQuery(id+"F0.wireOp",EDGE,"E15.11.0"),sQuery(id+"F0.wireOp",EDGE,"E15.11.1"),sQuery(id+"F0.wireOp",EDGE,"E15.11.2"),sQuery(id+"F0.wireOp",EDGE,"E15.11.3"),sQuery(id+"F0.wireOp",EDGE,"E16.bottom"),sQuery(id+"F0.wireOp",EDGE,"E16.top"),sQuery(id+"F0.wireOp",EDGE,"E16.left"),sQuery(id+"F0.wireOp",EDGE,"E16.right")])],"isStart":false});
            var sketch = newSketch(context, id + "F2", { "sketchPlane" : qUnion([Q0])});
            skCircle(sketch, "E17", {"center": v(0, 0) * mm, "radius": 11 * mm});
            skSolve(sketch);
        }
        {
            var Q0;
            Q0=qSketchRegion(id+"F2",true);
            extrude(context, id + "F3", {"entities" : qUnion([Q0]), "operationType" : NewBodyOperationType.REMOVE, "oppositeDirection" : true, "depth" : 25 * mm, "offsetDistance" : 25 * mm});
        }
        {
            var Q0;
            Q0 = qSketchRegion(id + "F2", true);
            extrude(context, id + "F4", {"entities" : qUnion([Q0]), "depth" : 80 * mm, "offsetDistance" : 25 * mm, "symmetric" : true});
        }
        {
            var Q0;
            Q0=makeQuery(id+"F1.opExtrude","CAP_FACE",FACE,{"disambiguationData":[OSD([sQuery(id+"F0.wireOp",EDGE,"E0"),sQuery(id+"F0.wireOp",EDGE,"E1"),sQuery(id+"F0.wireOp",EDGE,"E6"),sQuery(id+"F0.wireOp",EDGE,"E7.1.0"),sQuery(id+"F0.wireOp",EDGE,"E7.1.1"),sQuery(id+"F0.wireOp",EDGE,"E7.1.2"),sQuery(id+"F0.wireOp",EDGE,"E7.1.3"),sQuery(id+"F0.wireOp",EDGE,"E7.2.0"),sQuery(id+"F0.wireOp",EDGE,"E7.2.1"),sQuery(id+"F0.wireOp",EDGE,"E7.2.2"),sQuery(id+"F0.wireOp",EDGE,"E7.2.3"),sQuery(id+"F0.wireOp",EDGE,"E7.3.0"),sQuery(id+"F0.wireOp",EDGE,"E7.3.1"),sQuery(id+"F0.wireOp",EDGE,"E7.3.2"),sQuery(id+"F0.wireOp",EDGE,"E7.3.3"),sQuery(id+"F0.wireOp",EDGE,"E7.4.0"),sQuery(id+"F0.wireOp",EDGE,"E7.4.1"),sQuery(id+"F0.wireOp",EDGE,"E7.4.2"),sQuery(id+"F0.wireOp",EDGE,"E7.4.3"),sQuery(id+"F0.wireOp",EDGE,"E7.5.0"),sQuery(id+"F0.wireOp",EDGE,"E7.5.1"),sQuery(id+"F0.wireOp",EDGE,"E7.5.2"),sQuery(id+"F0.wireOp",EDGE,"E7.5.3"),sQuery(id+"F0.wireOp",EDGE,"E7.6.0"),sQuery(id+"F0.wireOp",EDGE,"E7.6.1"),sQuery(id+"F0.wireOp",EDGE,"E7.6.2"),sQuery(id+"F0.wireOp",EDGE,"E7.6.3"),sQuery(id+"F0.wireOp",EDGE,"E7.7.0"),sQuery(id+"F0.wireOp",EDGE,"E7.7.1"),sQuery(id+"F0.wireOp",EDGE,"E7.7.2"),sQuery(id+"F0.wireOp",EDGE,"E7.7.3"),sQuery(id+"F0.wireOp",EDGE,"E7.8.0"),sQuery(id+"F0.wireOp",EDGE,"E7.8.1"),sQuery(id+"F0.wireOp",EDGE,"E7.8.2"),sQuery(id+"F0.wireOp",EDGE,"E7.8.3"),sQuery(id+"F0.wireOp",EDGE,"E7.9.0"),sQuery(id+"F0.wireOp",EDGE,"E7.9.1"),sQuery(id+"F0.wireOp",EDGE,"E7.9.2"),sQuery(id+"F0.wireOp",EDGE,"E7.9.3"),sQuery(id+"F0.wireOp",EDGE,"E7.10.0"),sQuery(id+"F0.wireOp",EDGE,"E7.10.1"),sQuery(id+"F0.wireOp",EDGE,"E7.10.2"),sQuery(id+"F0.wireOp",EDGE,"E7.10.3"),sQuery(id+"F0.wireOp",EDGE,"E7.11.0"),sQuery(id+"F0.wireOp",EDGE,"E7.11.1"),sQuery(id+"F0.wireOp",EDGE,"E7.11.2"),sQuery(id+"F0.wireOp",EDGE,"E7.11.3"),sQuery(id+"F0.wireOp",EDGE,"E7.12.0"),sQuery(id+"F0.wireOp",EDGE,"E7.12.1"),sQuery(id+"F0.wireOp",EDGE,"E7.12.2"),sQuery(id+"F0.wireOp",EDGE,"E7.12.3"),sQuery(id+"F0.wireOp",EDGE,"E7.13.0"),sQuery(id+"F0.wireOp",EDGE,"E7.13.1"),sQuery(id+"F0.wireOp",EDGE,"E7.13.2"),sQuery(id+"F0.wireOp",EDGE,"E7.13.3"),sQuery(id+"F0.wireOp",EDGE,"E7.14.0"),sQuery(id+"F0.wireOp",EDGE,"E7.14.1"),sQuery(id+"F0.wireOp",EDGE,"E7.14.2"),sQuery(id+"F0.wireOp",EDGE,"E7.14.3"),sQuery(id+"F0.wireOp",EDGE,"E7.15.0"),sQuery(id+"F0.wireOp",EDGE,"E7.15.1"),sQuery(id+"F0.wireOp",EDGE,"E7.15.2"),sQuery(id+"F0.wireOp",EDGE,"E7.15.3"),sQuery(id+"F0.wireOp",EDGE,"E7.16.0"),sQuery(id+"F0.wireOp",EDGE,"E7.16.1"),sQuery(id+"F0.wireOp",EDGE,"E7.16.2"),sQuery(id+"F0.wireOp",EDGE,"E7.16.3"),sQuery(id+"F0.wireOp",EDGE,"E7.17.0"),sQuery(id+"F0.wireOp",EDGE,"E7.17.1"),sQuery(id+"F0.wireOp",EDGE,"E7.17.2"),sQuery(id+"F0.wireOp",EDGE,"E7.17.3"),sQuery(id+"F0.wireOp",EDGE,"E7.18.0"),sQuery(id+"F0.wireOp",EDGE,"E7.18.1"),sQuery(id+"F0.wireOp",EDGE,"E7.18.2"),sQuery(id+"F0.wireOp",EDGE,"E7.18.3"),sQuery(id+"F0.wireOp",EDGE,"E7.19.0"),sQuery(id+"F0.wireOp",EDGE,"E7.19.1"),sQuery(id+"F0.wireOp",EDGE,"E7.19.2"),sQuery(id+"F0.wireOp",EDGE,"E7.19.3"),sQuery(id+"F0.wireOp",EDGE,"E7.20.0"),sQuery(id+"F0.wireOp",EDGE,"E7.20.1"),sQuery(id+"F0.wireOp",EDGE,"E7.20.2"),sQuery(id+"F0.wireOp",EDGE,"E7.20.3"),sQuery(id+"F0.wireOp",EDGE,"E7.21.0"),sQuery(id+"F0.wireOp",EDGE,"E7.21.1"),sQuery(id+"F0.wireOp",EDGE,"E7.21.2"),sQuery(id+"F0.wireOp",EDGE,"E7.21.3"),sQuery(id+"F0.wireOp",EDGE,"E7.22.0"),sQuery(id+"F0.wireOp",EDGE,"E7.22.1"),sQuery(id+"F0.wireOp",EDGE,"E7.22.2"),sQuery(id+"F0.wireOp",EDGE,"E7.22.3"),sQuery(id+"F0.wireOp",EDGE,"E7.23.0"),sQuery(id+"F0.wireOp",EDGE,"E7.23.1"),sQuery(id+"F0.wireOp",EDGE,"E7.23.2"),sQuery(id+"F0.wireOp",EDGE,"E7.23.3"),sQuery(id+"F0.wireOp",EDGE,"E7.24.0"),sQuery(id+"F0.wireOp",EDGE,"E7.24.1"),sQuery(id+"F0.wireOp",EDGE,"E7.24.2"),sQuery(id+"F0.wireOp",EDGE,"E7.24.3"),sQuery(id+"F0.wireOp",EDGE,"E7.25.0"),sQuery(id+"F0.wireOp",EDGE,"E7.25.1"),sQuery(id+"F0.wireOp",EDGE,"E7.25.2"),sQuery(id+"F0.wireOp",EDGE,"E7.25.3"),sQuery(id+"F0.wireOp",EDGE,"E7.26.0"),sQuery(id+"F0.wireOp",EDGE,"E7.26.1"),sQuery(id+"F0.wireOp",EDGE,"E7.26.2"),sQuery(id+"F0.wireOp",EDGE,"E7.26.3"),sQuery(id+"F0.wireOp",EDGE,"E7.27.0"),sQuery(id+"F0.wireOp",EDGE,"E7.27.1"),sQuery(id+"F0.wireOp",EDGE,"E7.27.2"),sQuery(id+"F0.wireOp",EDGE,"E7.27.3"),sQuery(id+"F0.wireOp",EDGE,"E7.28.0"),sQuery(id+"F0.wireOp",EDGE,"E7.28.1"),sQuery(id+"F0.wireOp",EDGE,"E7.28.2"),sQuery(id+"F0.wireOp",EDGE,"E7.28.3"),sQuery(id+"F0.wireOp",EDGE,"E7.29.0"),sQuery(id+"F0.wireOp",EDGE,"E7.29.1"),sQuery(id+"F0.wireOp",EDGE,"E7.29.2"),sQuery(id+"F0.wireOp",EDGE,"E7.29.3"),sQuery(id+"F0.wireOp",EDGE,"E7.30.0"),sQuery(id+"F0.wireOp",EDGE,"E7.30.1"),sQuery(id+"F0.wireOp",EDGE,"E7.30.2"),sQuery(id+"F0.wireOp",EDGE,"E7.30.3"),sQuery(id+"F0.wireOp",EDGE,"E7.31.0"),sQuery(id+"F0.wireOp",EDGE,"E7.31.1"),sQuery(id+"F0.wireOp",EDGE,"E7.31.2"),sQuery(id+"F0.wireOp",EDGE,"E7.31.3"),sQuery(id+"F0.wireOp",EDGE,"E7.32.0"),sQuery(id+"F0.wireOp",EDGE,"E7.32.1"),sQuery(id+"F0.wireOp",EDGE,"E7.32.2"),sQuery(id+"F0.wireOp",EDGE,"E7.32.3"),sQuery(id+"F0.wireOp",EDGE,"E7.33.0"),sQuery(id+"F0.wireOp",EDGE,"E7.33.1"),sQuery(id+"F0.wireOp",EDGE,"E7.33.2"),sQuery(id+"F0.wireOp",EDGE,"E7.33.3"),sQuery(id+"F0.wireOp",EDGE,"E7.34.0"),sQuery(id+"F0.wireOp",EDGE,"E7.34.1"),sQuery(id+"F0.wireOp",EDGE,"E7.34.2"),sQuery(id+"F0.wireOp",EDGE,"E7.34.3"),sQuery(id+"F0.wireOp",EDGE,"E7.35.0"),sQuery(id+"F0.wireOp",EDGE,"E7.35.1"),sQuery(id+"F0.wireOp",EDGE,"E7.35.2"),sQuery(id+"F0.wireOp",EDGE,"E7.35.3"),sQuery(id+"F0.wireOp",EDGE,"E7.36.0"),sQuery(id+"F0.wireOp",EDGE,"E7.36.1"),sQuery(id+"F0.wireOp",EDGE,"E7.36.2"),sQuery(id+"F0.wireOp",EDGE,"E7.36.3"),sQuery(id+"F0.wireOp",EDGE,"E7.37.0"),sQuery(id+"F0.wireOp",EDGE,"E7.37.1"),sQuery(id+"F0.wireOp",EDGE,"E7.37.2"),sQuery(id+"F0.wireOp",EDGE,"E7.37.3"),sQuery(id+"F0.wireOp",EDGE,"E7.38.0"),sQuery(id+"F0.wireOp",EDGE,"E7.38.1"),sQuery(id+"F0.wireOp",EDGE,"E7.38.2"),sQuery(id+"F0.wireOp",EDGE,"E7.38.3"),sQuery(id+"F0.wireOp",EDGE,"E7.39.0"),sQuery(id+"F0.wireOp",EDGE,"E7.39.1"),sQuery(id+"F0.wireOp",EDGE,"E7.39.2"),sQuery(id+"F0.wireOp",EDGE,"E7.39.3"),sQuery(id+"F0.wireOp",EDGE,"E8"),sQuery(id+"F0.wireOp",EDGE,"E9"),sQuery(id+"F0.wireOp",EDGE,"E10"),sQuery(id+"F0.wireOp",EDGE,"E12.trimOffspring"),sQuery(id+"F0.wireOp",EDGE,"E13.trimOffspring"),sQuery(id+"F0.wireOp",EDGE,"E14.trimOffspring"),sQuery(id+"F0.wireOp",EDGE,"E15.1.0"),sQuery(id+"F0.wireOp",EDGE,"E15.1.1"),sQuery(id+"F0.wireOp",EDGE,"E15.1.2"),sQuery(id+"F0.wireOp",EDGE,"E15.1.3"),sQuery(id+"F0.wireOp",EDGE,"E15.2.0"),sQuery(id+"F0.wireOp",EDGE,"E15.2.1"),sQuery(id+"F0.wireOp",EDGE,"E15.2.2"),sQuery(id+"F0.wireOp",EDGE,"E15.2.3"),sQuery(id+"F0.wireOp",EDGE,"E15.3.0"),sQuery(id+"F0.wireOp",EDGE,"E15.3.1"),sQuery(id+"F0.wireOp",EDGE,"E15.3.2"),sQuery(id+"F0.wireOp",EDGE,"E15.3.3"),sQuery(id+"F0.wireOp",EDGE,"E15.4.0"),sQuery(id+"F0.wireOp",EDGE,"E15.4.1"),sQuery(id+"F0.wireOp",EDGE,"E15.4.2"),sQuery(id+"F0.wireOp",EDGE,"E15.4.3"),sQuery(id+"F0.wireOp",EDGE,"E15.5.0"),sQuery(id+"F0.wireOp",EDGE,"E15.5.1"),sQuery(id+"F0.wireOp",EDGE,"E15.5.2"),sQuery(id+"F0.wireOp",EDGE,"E15.5.3"),sQuery(id+"F0.wireOp",EDGE,"E15.6.0"),sQuery(id+"F0.wireOp",EDGE,"E15.6.1"),sQuery(id+"F0.wireOp",EDGE,"E15.6.2"),sQuery(id+"F0.wireOp",EDGE,"E15.6.3"),sQuery(id+"F0.wireOp",EDGE,"E15.7.0"),sQuery(id+"F0.wireOp",EDGE,"E15.7.1"),sQuery(id+"F0.wireOp",EDGE,"E15.7.2"),sQuery(id+"F0.wireOp",EDGE,"E15.7.3"),sQuery(id+"F0.wireOp",EDGE,"E15.8.0"),sQuery(id+"F0.wireOp",EDGE,"E15.8.1"),sQuery(id+"F0.wireOp",EDGE,"E15.8.2"),sQuery(id+"F0.wireOp",EDGE,"E15.8.3"),sQuery(id+"F0.wireOp",EDGE,"E15.9.0"),sQuery(id+"F0.wireOp",EDGE,"E15.9.1"),sQuery(id+"F0.wireOp",EDGE,"E15.9.2"),sQuery(id+"F0.wireOp",EDGE,"E15.9.3"),sQuery(id+"F0.wireOp",EDGE,"E15.10.0"),sQuery(id+"F0.wireOp",EDGE,"E15.10.1"),sQuery(id+"F0.wireOp",EDGE,"E15.10.2"),sQuery(id+"F0.wireOp",EDGE,"E15.10.3"),sQuery(id+"F0.wireOp",EDGE,"E15.11.0"),sQuery(id+"F0.wireOp",EDGE,"E15.11.1"),sQuery(id+"F0.wireOp",EDGE,"E15.11.2"),sQuery(id+"F0.wireOp",EDGE,"E15.11.3"),sQuery(id+"F0.wireOp",EDGE,"E16.bottom"),sQuery(id+"F0.wireOp",EDGE,"E16.top"),sQuery(id+"F0.wireOp",EDGE,"E16.left"),sQuery(id+"F0.wireOp",EDGE,"E16.right")])],"isStart":false});
            var sketch = newSketch(context, id + "F5", { "sketchPlane" : qUnion([Q0])});
            skCircle(sketch, "E18", {"center": v(0, 0) * mm, "radius": 143.62 * mm});
            skCircle(sketch, "E19", {"center": v(0, 0) * mm, "radius": 11 * mm});
            skSolve(sketch);
        }
        {
            var Q0;
            Q0 = qSketchRegion(id + "F5", true);
            extrude(context, id + "F6", {"entities" : qUnion([Q0]), "operationType" : NewBodyOperationType.ADD, "oppositeDirection" : true, "depth" : 5 * mm, "offsetDistance" : 25 * mm});
        }
        {
            var Q0;
            Q0=makeQuery(id+"F6.boolean.opBoolean","MERGE",FACE,{"derivedFrom":[makeQuery(id+"F1.opExtrude","CAP_FACE",FACE,{"disambiguationData":[OSD([sQuery(id+"F0.wireOp",EDGE,"E0"),sQuery(id+"F0.wireOp",EDGE,"E1"),sQuery(id+"F0.wireOp",EDGE,"E6"),sQuery(id+"F0.wireOp",EDGE,"E7.1.0"),sQuery(id+"F0.wireOp",EDGE,"E7.1.1"),sQuery(id+"F0.wireOp",EDGE,"E7.1.2"),sQuery(id+"F0.wireOp",EDGE,"E7.1.3"),sQuery(id+"F0.wireOp",EDGE,"E7.2.0"),sQuery(id+"F0.wireOp",EDGE,"E7.2.1"),sQuery(id+"F0.wireOp",EDGE,"E7.2.2"),sQuery(id+"F0.wireOp",EDGE,"E7.2.3"),sQuery(id+"F0.wireOp",EDGE,"E7.3.0"),sQuery(id+"F0.wireOp",EDGE,"E7.3.1"),sQuery(id+"F0.wireOp",EDGE,"E7.3.2"),sQuery(id+"F0.wireOp",EDGE,"E7.3.3"),sQuery(id+"F0.wireOp",EDGE,"E7.4.0"),sQuery(id+"F0.wireOp",EDGE,"E7.4.1"),sQuery(id+"F0.wireOp",EDGE,"E7.4.2"),sQuery(id+"F0.wireOp",EDGE,"E7.4.3"),sQuery(id+"F0.wireOp",EDGE,"E7.5.0"),sQuery(id+"F0.wireOp",EDGE,"E7.5.1"),sQuery(id+"F0.wireOp",EDGE,"E7.5.2"),sQuery(id+"F0.wireOp",EDGE,"E7.5.3"),sQuery(id+"F0.wireOp",EDGE,"E7.6.0"),sQuery(id+"F0.wireOp",EDGE,"E7.6.1"),sQuery(id+"F0.wireOp",EDGE,"E7.6.2"),sQuery(id+"F0.wireOp",EDGE,"E7.6.3"),sQuery(id+"F0.wireOp",EDGE,"E7.7.0"),sQuery(id+"F0.wireOp",EDGE,"E7.7.1"),sQuery(id+"F0.wireOp",EDGE,"E7.7.2"),sQuery(id+"F0.wireOp",EDGE,"E7.7.3"),sQuery(id+"F0.wireOp",EDGE,"E7.8.0"),sQuery(id+"F0.wireOp",EDGE,"E7.8.1"),sQuery(id+"F0.wireOp",EDGE,"E7.8.2"),sQuery(id+"F0.wireOp",EDGE,"E7.8.3"),sQuery(id+"F0.wireOp",EDGE,"E7.9.0"),sQuery(id+"F0.wireOp",EDGE,"E7.9.1"),sQuery(id+"F0.wireOp",EDGE,"E7.9.2"),sQuery(id+"F0.wireOp",EDGE,"E7.9.3"),sQuery(id+"F0.wireOp",EDGE,"E7.10.0"),sQuery(id+"F0.wireOp",EDGE,"E7.10.1"),sQuery(id+"F0.wireOp",EDGE,"E7.10.2"),sQuery(id+"F0.wireOp",EDGE,"E7.10.3"),sQuery(id+"F0.wireOp",EDGE,"E7.11.0"),sQuery(id+"F0.wireOp",EDGE,"E7.11.1"),sQuery(id+"F0.wireOp",EDGE,"E7.11.2"),sQuery(id+"F0.wireOp",EDGE,"E7.11.3"),sQuery(id+"F0.wireOp",EDGE,"E7.12.0"),sQuery(id+"F0.wireOp",EDGE,"E7.12.1"),sQuery(id+"F0.wireOp",EDGE,"E7.12.2"),sQuery(id+"F0.wireOp",EDGE,"E7.12.3"),sQuery(id+"F0.wireOp",EDGE,"E7.13.0"),sQuery(id+"F0.wireOp",EDGE,"E7.13.1"),sQuery(id+"F0.wireOp",EDGE,"E7.13.2"),sQuery(id+"F0.wireOp",EDGE,"E7.13.3"),sQuery(id+"F0.wireOp",EDGE,"E7.14.0"),sQuery(id+"F0.wireOp",EDGE,"E7.14.1"),sQuery(id+"F0.wireOp",EDGE,"E7.14.2"),sQuery(id+"F0.wireOp",EDGE,"E7.14.3"),sQuery(id+"F0.wireOp",EDGE,"E7.15.0"),sQuery(id+"F0.wireOp",EDGE,"E7.15.1"),sQuery(id+"F0.wireOp",EDGE,"E7.15.2"),sQuery(id+"F0.wireOp",EDGE,"E7.15.3"),sQuery(id+"F0.wireOp",EDGE,"E7.16.0"),sQuery(id+"F0.wireOp",EDGE,"E7.16.1"),sQuery(id+"F0.wireOp",EDGE,"E7.16.2"),sQuery(id+"F0.wireOp",EDGE,"E7.16.3"),sQuery(id+"F0.wireOp",EDGE,"E7.17.0"),sQuery(id+"F0.wireOp",EDGE,"E7.17.1"),sQuery(id+"F0.wireOp",EDGE,"E7.17.2"),sQuery(id+"F0.wireOp",EDGE,"E7.17.3"),sQuery(id+"F0.wireOp",EDGE,"E7.18.0"),sQuery(id+"F0.wireOp",EDGE,"E7.18.1"),sQuery(id+"F0.wireOp",EDGE,"E7.18.2"),sQuery(id+"F0.wireOp",EDGE,"E7.18.3"),sQuery(id+"F0.wireOp",EDGE,"E7.19.0"),sQuery(id+"F0.wireOp",EDGE,"E7.19.1"),sQuery(id+"F0.wireOp",EDGE,"E7.19.2"),sQuery(id+"F0.wireOp",EDGE,"E7.19.3"),sQuery(id+"F0.wireOp",EDGE,"E7.20.0"),sQuery(id+"F0.wireOp",EDGE,"E7.20.1"),sQuery(id+"F0.wireOp",EDGE,"E7.20.2"),sQuery(id+"F0.wireOp",EDGE,"E7.20.3"),sQuery(id+"F0.wireOp",EDGE,"E7.21.0"),sQuery(id+"F0.wireOp",EDGE,"E7.21.1"),sQuery(id+"F0.wireOp",EDGE,"E7.21.2"),sQuery(id+"F0.wireOp",EDGE,"E7.21.3"),sQuery(id+"F0.wireOp",EDGE,"E7.22.0"),sQuery(id+"F0.wireOp",EDGE,"E7.22.1"),sQuery(id+"F0.wireOp",EDGE,"E7.22.2"),sQuery(id+"F0.wireOp",EDGE,"E7.22.3"),sQuery(id+"F0.wireOp",EDGE,"E7.23.0"),sQuery(id+"F0.wireOp",EDGE,"E7.23.1"),sQuery(id+"F0.wireOp",EDGE,"E7.23.2"),sQuery(id+"F0.wireOp",EDGE,"E7.23.3"),sQuery(id+"F0.wireOp",EDGE,"E7.24.0"),sQuery(id+"F0.wireOp",EDGE,"E7.24.1"),sQuery(id+"F0.wireOp",EDGE,"E7.24.2"),sQuery(id+"F0.wireOp",EDGE,"E7.24.3"),sQuery(id+"F0.wireOp",EDGE,"E7.25.0"),sQuery(id+"F0.wireOp",EDGE,"E7.25.1"),sQuery(id+"F0.wireOp",EDGE,"E7.25.2"),sQuery(id+"F0.wireOp",EDGE,"E7.25.3"),sQuery(id+"F0.wireOp",EDGE,"E7.26.0"),sQuery(id+"F0.wireOp",EDGE,"E7.26.1"),sQuery(id+"F0.wireOp",EDGE,"E7.26.2"),sQuery(id+"F0.wireOp",EDGE,"E7.26.3"),sQuery(id+"F0.wireOp",EDGE,"E7.27.0"),sQuery(id+"F0.wireOp",EDGE,"E7.27.1"),sQuery(id+"F0.wireOp",EDGE,"E7.27.2"),sQuery(id+"F0.wireOp",EDGE,"E7.27.3"),sQuery(id+"F0.wireOp",EDGE,"E7.28.0"),sQuery(id+"F0.wireOp",EDGE,"E7.28.1"),sQuery(id+"F0.wireOp",EDGE,"E7.28.2"),sQuery(id+"F0.wireOp",EDGE,"E7.28.3"),sQuery(id+"F0.wireOp",EDGE,"E7.29.0"),sQuery(id+"F0.wireOp",EDGE,"E7.29.1"),sQuery(id+"F0.wireOp",EDGE,"E7.29.2"),sQuery(id+"F0.wireOp",EDGE,"E7.29.3"),sQuery(id+"F0.wireOp",EDGE,"E7.30.0"),sQuery(id+"F0.wireOp",EDGE,"E7.30.1"),sQuery(id+"F0.wireOp",EDGE,"E7.30.2"),sQuery(id+"F0.wireOp",EDGE,"E7.30.3"),sQuery(id+"F0.wireOp",EDGE,"E7.31.0"),sQuery(id+"F0.wireOp",EDGE,"E7.31.1"),sQuery(id+"F0.wireOp",EDGE,"E7.31.2"),sQuery(id+"F0.wireOp",EDGE,"E7.31.3"),sQuery(id+"F0.wireOp",EDGE,"E7.32.0"),sQuery(id+"F0.wireOp",EDGE,"E7.32.1"),sQuery(id+"F0.wireOp",EDGE,"E7.32.2"),sQuery(id+"F0.wireOp",EDGE,"E7.32.3"),sQuery(id+"F0.wireOp",EDGE,"E7.33.0"),sQuery(id+"F0.wireOp",EDGE,"E7.33.1"),sQuery(id+"F0.wireOp",EDGE,"E7.33.2"),sQuery(id+"F0.wireOp",EDGE,"E7.33.3"),sQuery(id+"F0.wireOp",EDGE,"E7.34.0"),sQuery(id+"F0.wireOp",EDGE,"E7.34.1"),sQuery(id+"F0.wireOp",EDGE,"E7.34.2"),sQuery(id+"F0.wireOp",EDGE,"E7.34.3"),sQuery(id+"F0.wireOp",EDGE,"E7.35.0"),sQuery(id+"F0.wireOp",EDGE,"E7.35.1"),sQuery(id+"F0.wireOp",EDGE,"E7.35.2"),sQuery(id+"F0.wireOp",EDGE,"E7.35.3"),sQuery(id+"F0.wireOp",EDGE,"E7.36.0"),sQuery(id+"F0.wireOp",EDGE,"E7.36.1"),sQuery(id+"F0.wireOp",EDGE,"E7.36.2"),sQuery(id+"F0.wireOp",EDGE,"E7.36.3"),sQuery(id+"F0.wireOp",EDGE,"E7.37.0"),sQuery(id+"F0.wireOp",EDGE,"E7.37.1"),sQuery(id+"F0.wireOp",EDGE,"E7.37.2"),sQuery(id+"F0.wireOp",EDGE,"E7.37.3"),sQuery(id+"F0.wireOp",EDGE,"E7.38.0"),sQuery(id+"F0.wireOp",EDGE,"E7.38.1"),sQuery(id+"F0.wireOp",EDGE,"E7.38.2"),sQuery(id+"F0.wireOp",EDGE,"E7.38.3"),sQuery(id+"F0.wireOp",EDGE,"E7.39.0"),sQuery(id+"F0.wireOp",EDGE,"E7.39.1"),sQuery(id+"F0.wireOp",EDGE,"E7.39.2"),sQuery(id+"F0.wireOp",EDGE,"E7.39.3"),sQuery(id+"F0.wireOp",EDGE,"E8"),sQuery(id+"F0.wireOp",EDGE,"E9"),sQuery(id+"F0.wireOp",EDGE,"E10"),sQuery(id+"F0.wireOp",EDGE,"E12.trimOffspring"),sQuery(id+"F0.wireOp",EDGE,"E13.trimOffspring"),sQuery(id+"F0.wireOp",EDGE,"E14.trimOffspring"),sQuery(id+"F0.wireOp",EDGE,"E15.1.0"),sQuery(id+"F0.wireOp",EDGE,"E15.1.1"),sQuery(id+"F0.wireOp",EDGE,"E15.1.2"),sQuery(id+"F0.wireOp",EDGE,"E15.1.3"),sQuery(id+"F0.wireOp",EDGE,"E15.2.0"),sQuery(id+"F0.wireOp",EDGE,"E15.2.1"),sQuery(id+"F0.wireOp",EDGE,"E15.2.2"),sQuery(id+"F0.wireOp",EDGE,"E15.2.3"),sQuery(id+"F0.wireOp",EDGE,"E15.3.0"),sQuery(id+"F0.wireOp",EDGE,"E15.3.1"),sQuery(id+"F0.wireOp",EDGE,"E15.3.2"),sQuery(id+"F0.wireOp",EDGE,"E15.3.3"),sQuery(id+"F0.wireOp",EDGE,"E15.4.0"),sQuery(id+"F0.wireOp",EDGE,"E15.4.1"),sQuery(id+"F0.wireOp",EDGE,"E15.4.2"),sQuery(id+"F0.wireOp",EDGE,"E15.4.3"),sQuery(id+"F0.wireOp",EDGE,"E15.5.0"),sQuery(id+"F0.wireOp",EDGE,"E15.5.1"),sQuery(id+"F0.wireOp",EDGE,"E15.5.2"),sQuery(id+"F0.wireOp",EDGE,"E15.5.3"),sQuery(id+"F0.wireOp",EDGE,"E15.6.0"),sQuery(id+"F0.wireOp",EDGE,"E15.6.1"),sQuery(id+"F0.wireOp",EDGE,"E15.6.2"),sQuery(id+"F0.wireOp",EDGE,"E15.6.3"),sQuery(id+"F0.wireOp",EDGE,"E15.7.0"),sQuery(id+"F0.wireOp",EDGE,"E15.7.1"),sQuery(id+"F0.wireOp",EDGE,"E15.7.2"),sQuery(id+"F0.wireOp",EDGE,"E15.7.3"),sQuery(id+"F0.wireOp",EDGE,"E15.8.0"),sQuery(id+"F0.wireOp",EDGE,"E15.8.1"),sQuery(id+"F0.wireOp",EDGE,"E15.8.2"),sQuery(id+"F0.wireOp",EDGE,"E15.8.3"),sQuery(id+"F0.wireOp",EDGE,"E15.9.0"),sQuery(id+"F0.wireOp",EDGE,"E15.9.1"),sQuery(id+"F0.wireOp",EDGE,"E15.9.2"),sQuery(id+"F0.wireOp",EDGE,"E15.9.3"),sQuery(id+"F0.wireOp",EDGE,"E15.10.0"),sQuery(id+"F0.wireOp",EDGE,"E15.10.1"),sQuery(id+"F0.wireOp",EDGE,"E15.10.2"),sQuery(id+"F0.wireOp",EDGE,"E15.10.3"),sQuery(id+"F0.wireOp",EDGE,"E15.11.0"),sQuery(id+"F0.wireOp",EDGE,"E15.11.1"),sQuery(id+"F0.wireOp",EDGE,"E15.11.2"),sQuery(id+"F0.wireOp",EDGE,"E15.11.3"),sQuery(id+"F0.wireOp",EDGE,"E16.bottom"),sQuery(id+"F0.wireOp",EDGE,"E16.top"),sQuery(id+"F0.wireOp",EDGE,"E16.left"),sQuery(id+"F0.wireOp",EDGE,"E16.right")])],"isStart":false}),makeQuery(id+"F6.opExtrude","CAP_FACE",FACE,{"disambiguationData":[OSD([sQuery(id+"F5.wireOp",EDGE,"E18"),sQuery(id+"F5.wireOp",EDGE,"E19")])],"isStart":true})]});
            var sketch = newSketch(context, id + "F7", { "sketchPlane" : qUnion([Q0])});
            skCircle(sketch, "E20", {"center": v(0, 0) * mm, "radius": 17.5 * mm});
            skSolve(sketch);
        }
        {
            var Q0;
            Q0 = qSketchRegion(id + "F7", true);
            extrude(context, id + "F8", {"entities" : qUnion([Q0]), "operationType" : NewBodyOperationType.REMOVE, "oppositeDirection" : true, "depth" : 25 * mm, "offsetDistance" : 25 * mm});
        }
        {
            var Q0;
            Q0=makeQuery(id+"F6.boolean.opBoolean","MERGE",FACE,{"derivedFrom":[makeQuery(id+"F1.opExtrude","CAP_FACE",FACE,{"disambiguationData":[OSD([sQuery(id+"F0.wireOp",EDGE,"E0"),sQuery(id+"F0.wireOp",EDGE,"E1"),sQuery(id+"F0.wireOp",EDGE,"E6"),sQuery(id+"F0.wireOp",EDGE,"E7.1.0"),sQuery(id+"F0.wireOp",EDGE,"E7.1.1"),sQuery(id+"F0.wireOp",EDGE,"E7.1.2"),sQuery(id+"F0.wireOp",EDGE,"E7.1.3"),sQuery(id+"F0.wireOp",EDGE,"E7.2.0"),sQuery(id+"F0.wireOp",EDGE,"E7.2.1"),sQuery(id+"F0.wireOp",EDGE,"E7.2.2"),sQuery(id+"F0.wireOp",EDGE,"E7.2.3"),sQuery(id+"F0.wireOp",EDGE,"E7.3.0"),sQuery(id+"F0.wireOp",EDGE,"E7.3.1"),sQuery(id+"F0.wireOp",EDGE,"E7.3.2"),sQuery(id+"F0.wireOp",EDGE,"E7.3.3"),sQuery(id+"F0.wireOp",EDGE,"E7.4.0"),sQuery(id+"F0.wireOp",EDGE,"E7.4.1"),sQuery(id+"F0.wireOp",EDGE,"E7.4.2"),sQuery(id+"F0.wireOp",EDGE,"E7.4.3"),sQuery(id+"F0.wireOp",EDGE,"E7.5.0"),sQuery(id+"F0.wireOp",EDGE,"E7.5.1"),sQuery(id+"F0.wireOp",EDGE,"E7.5.2"),sQuery(id+"F0.wireOp",EDGE,"E7.5.3"),sQuery(id+"F0.wireOp",EDGE,"E7.6.0"),sQuery(id+"F0.wireOp",EDGE,"E7.6.1"),sQuery(id+"F0.wireOp",EDGE,"E7.6.2"),sQuery(id+"F0.wireOp",EDGE,"E7.6.3"),sQuery(id+"F0.wireOp",EDGE,"E7.7.0"),sQuery(id+"F0.wireOp",EDGE,"E7.7.1"),sQuery(id+"F0.wireOp",EDGE,"E7.7.2"),sQuery(id+"F0.wireOp",EDGE,"E7.7.3"),sQuery(id+"F0.wireOp",EDGE,"E7.8.0"),sQuery(id+"F0.wireOp",EDGE,"E7.8.1"),sQuery(id+"F0.wireOp",EDGE,"E7.8.2"),sQuery(id+"F0.wireOp",EDGE,"E7.8.3"),sQuery(id+"F0.wireOp",EDGE,"E7.9.0"),sQuery(id+"F0.wireOp",EDGE,"E7.9.1"),sQuery(id+"F0.wireOp",EDGE,"E7.9.2"),sQuery(id+"F0.wireOp",EDGE,"E7.9.3"),sQuery(id+"F0.wireOp",EDGE,"E7.10.0"),sQuery(id+"F0.wireOp",EDGE,"E7.10.1"),sQuery(id+"F0.wireOp",EDGE,"E7.10.2"),sQuery(id+"F0.wireOp",EDGE,"E7.10.3"),sQuery(id+"F0.wireOp",EDGE,"E7.11.0"),sQuery(id+"F0.wireOp",EDGE,"E7.11.1"),sQuery(id+"F0.wireOp",EDGE,"E7.11.2"),sQuery(id+"F0.wireOp",EDGE,"E7.11.3"),sQuery(id+"F0.wireOp",EDGE,"E7.12.0"),sQuery(id+"F0.wireOp",EDGE,"E7.12.1"),sQuery(id+"F0.wireOp",EDGE,"E7.12.2"),sQuery(id+"F0.wireOp",EDGE,"E7.12.3"),sQuery(id+"F0.wireOp",EDGE,"E7.13.0"),sQuery(id+"F0.wireOp",EDGE,"E7.13.1"),sQuery(id+"F0.wireOp",EDGE,"E7.13.2"),sQuery(id+"F0.wireOp",EDGE,"E7.13.3"),sQuery(id+"F0.wireOp",EDGE,"E7.14.0"),sQuery(id+"F0.wireOp",EDGE,"E7.14.1"),sQuery(id+"F0.wireOp",EDGE,"E7.14.2"),sQuery(id+"F0.wireOp",EDGE,"E7.14.3"),sQuery(id+"F0.wireOp",EDGE,"E7.15.0"),sQuery(id+"F0.wireOp",EDGE,"E7.15.1"),sQuery(id+"F0.wireOp",EDGE,"E7.15.2"),sQuery(id+"F0.wireOp",EDGE,"E7.15.3"),sQuery(id+"F0.wireOp",EDGE,"E7.16.0"),sQuery(id+"F0.wireOp",EDGE,"E7.16.1"),sQuery(id+"F0.wireOp",EDGE,"E7.16.2"),sQuery(id+"F0.wireOp",EDGE,"E7.16.3"),sQuery(id+"F0.wireOp",EDGE,"E7.17.0"),sQuery(id+"F0.wireOp",EDGE,"E7.17.1"),sQuery(id+"F0.wireOp",EDGE,"E7.17.2"),sQuery(id+"F0.wireOp",EDGE,"E7.17.3"),sQuery(id+"F0.wireOp",EDGE,"E7.18.0"),sQuery(id+"F0.wireOp",EDGE,"E7.18.1"),sQuery(id+"F0.wireOp",EDGE,"E7.18.2"),sQuery(id+"F0.wireOp",EDGE,"E7.18.3"),sQuery(id+"F0.wireOp",EDGE,"E7.19.0"),sQuery(id+"F0.wireOp",EDGE,"E7.19.1"),sQuery(id+"F0.wireOp",EDGE,"E7.19.2"),sQuery(id+"F0.wireOp",EDGE,"E7.19.3"),sQuery(id+"F0.wireOp",EDGE,"E7.20.0"),sQuery(id+"F0.wireOp",EDGE,"E7.20.1"),sQuery(id+"F0.wireOp",EDGE,"E7.20.2"),sQuery(id+"F0.wireOp",EDGE,"E7.20.3"),sQuery(id+"F0.wireOp",EDGE,"E7.21.0"),sQuery(id+"F0.wireOp",EDGE,"E7.21.1"),sQuery(id+"F0.wireOp",EDGE,"E7.21.2"),sQuery(id+"F0.wireOp",EDGE,"E7.21.3"),sQuery(id+"F0.wireOp",EDGE,"E7.22.0"),sQuery(id+"F0.wireOp",EDGE,"E7.22.1"),sQuery(id+"F0.wireOp",EDGE,"E7.22.2"),sQuery(id+"F0.wireOp",EDGE,"E7.22.3"),sQuery(id+"F0.wireOp",EDGE,"E7.23.0"),sQuery(id+"F0.wireOp",EDGE,"E7.23.1"),sQuery(id+"F0.wireOp",EDGE,"E7.23.2"),sQuery(id+"F0.wireOp",EDGE,"E7.23.3"),sQuery(id+"F0.wireOp",EDGE,"E7.24.0"),sQuery(id+"F0.wireOp",EDGE,"E7.24.1"),sQuery(id+"F0.wireOp",EDGE,"E7.24.2"),sQuery(id+"F0.wireOp",EDGE,"E7.24.3"),sQuery(id+"F0.wireOp",EDGE,"E7.25.0"),sQuery(id+"F0.wireOp",EDGE,"E7.25.1"),sQuery(id+"F0.wireOp",EDGE,"E7.25.2"),sQuery(id+"F0.wireOp",EDGE,"E7.25.3"),sQuery(id+"F0.wireOp",EDGE,"E7.26.0"),sQuery(id+"F0.wireOp",EDGE,"E7.26.1"),sQuery(id+"F0.wireOp",EDGE,"E7.26.2"),sQuery(id+"F0.wireOp",EDGE,"E7.26.3"),sQuery(id+"F0.wireOp",EDGE,"E7.27.0"),sQuery(id+"F0.wireOp",EDGE,"E7.27.1"),sQuery(id+"F0.wireOp",EDGE,"E7.27.2"),sQuery(id+"F0.wireOp",EDGE,"E7.27.3"),sQuery(id+"F0.wireOp",EDGE,"E7.28.0"),sQuery(id+"F0.wireOp",EDGE,"E7.28.1"),sQuery(id+"F0.wireOp",EDGE,"E7.28.2"),sQuery(id+"F0.wireOp",EDGE,"E7.28.3"),sQuery(id+"F0.wireOp",EDGE,"E7.29.0"),sQuery(id+"F0.wireOp",EDGE,"E7.29.1"),sQuery(id+"F0.wireOp",EDGE,"E7.29.2"),sQuery(id+"F0.wireOp",EDGE,"E7.29.3"),sQuery(id+"F0.wireOp",EDGE,"E7.30.0"),sQuery(id+"F0.wireOp",EDGE,"E7.30.1"),sQuery(id+"F0.wireOp",EDGE,"E7.30.2"),sQuery(id+"F0.wireOp",EDGE,"E7.30.3"),sQuery(id+"F0.wireOp",EDGE,"E7.31.0"),sQuery(id+"F0.wireOp",EDGE,"E7.31.1"),sQuery(id+"F0.wireOp",EDGE,"E7.31.2"),sQuery(id+"F0.wireOp",EDGE,"E7.31.3"),sQuery(id+"F0.wireOp",EDGE,"E7.32.0"),sQuery(id+"F0.wireOp",EDGE,"E7.32.1"),sQuery(id+"F0.wireOp",EDGE,"E7.32.2"),sQuery(id+"F0.wireOp",EDGE,"E7.32.3"),sQuery(id+"F0.wireOp",EDGE,"E7.33.0"),sQuery(id+"F0.wireOp",EDGE,"E7.33.1"),sQuery(id+"F0.wireOp",EDGE,"E7.33.2"),sQuery(id+"F0.wireOp",EDGE,"E7.33.3"),sQuery(id+"F0.wireOp",EDGE,"E7.34.0"),sQuery(id+"F0.wireOp",EDGE,"E7.34.1"),sQuery(id+"F0.wireOp",EDGE,"E7.34.2"),sQuery(id+"F0.wireOp",EDGE,"E7.34.3"),sQuery(id+"F0.wireOp",EDGE,"E7.35.0"),sQuery(id+"F0.wireOp",EDGE,"E7.35.1"),sQuery(id+"F0.wireOp",EDGE,"E7.35.2"),sQuery(id+"F0.wireOp",EDGE,"E7.35.3"),sQuery(id+"F0.wireOp",EDGE,"E7.36.0"),sQuery(id+"F0.wireOp",EDGE,"E7.36.1"),sQuery(id+"F0.wireOp",EDGE,"E7.36.2"),sQuery(id+"F0.wireOp",EDGE,"E7.36.3"),sQuery(id+"F0.wireOp",EDGE,"E7.37.0"),sQuery(id+"F0.wireOp",EDGE,"E7.37.1"),sQuery(id+"F0.wireOp",EDGE,"E7.37.2"),sQuery(id+"F0.wireOp",EDGE,"E7.37.3"),sQuery(id+"F0.wireOp",EDGE,"E7.38.0"),sQuery(id+"F0.wireOp",EDGE,"E7.38.1"),sQuery(id+"F0.wireOp",EDGE,"E7.38.2"),sQuery(id+"F0.wireOp",EDGE,"E7.38.3"),sQuery(id+"F0.wireOp",EDGE,"E7.39.0"),sQuery(id+"F0.wireOp",EDGE,"E7.39.1"),sQuery(id+"F0.wireOp",EDGE,"E7.39.2"),sQuery(id+"F0.wireOp",EDGE,"E7.39.3"),sQuery(id+"F0.wireOp",EDGE,"E8"),sQuery(id+"F0.wireOp",EDGE,"E9"),sQuery(id+"F0.wireOp",EDGE,"E10"),sQuery(id+"F0.wireOp",EDGE,"E12.trimOffspring"),sQuery(id+"F0.wireOp",EDGE,"E13.trimOffspring"),sQuery(id+"F0.wireOp",EDGE,"E14.trimOffspring"),sQuery(id+"F0.wireOp",EDGE,"E15.1.0"),sQuery(id+"F0.wireOp",EDGE,"E15.1.1"),sQuery(id+"F0.wireOp",EDGE,"E15.1.2"),sQuery(id+"F0.wireOp",EDGE,"E15.1.3"),sQuery(id+"F0.wireOp",EDGE,"E15.2.0"),sQuery(id+"F0.wireOp",EDGE,"E15.2.1"),sQuery(id+"F0.wireOp",EDGE,"E15.2.2"),sQuery(id+"F0.wireOp",EDGE,"E15.2.3"),sQuery(id+"F0.wireOp",EDGE,"E15.3.0"),sQuery(id+"F0.wireOp",EDGE,"E15.3.1"),sQuery(id+"F0.wireOp",EDGE,"E15.3.2"),sQuery(id+"F0.wireOp",EDGE,"E15.3.3"),sQuery(id+"F0.wireOp",EDGE,"E15.4.0"),sQuery(id+"F0.wireOp",EDGE,"E15.4.1"),sQuery(id+"F0.wireOp",EDGE,"E15.4.2"),sQuery(id+"F0.wireOp",EDGE,"E15.4.3"),sQuery(id+"F0.wireOp",EDGE,"E15.5.0"),sQuery(id+"F0.wireOp",EDGE,"E15.5.1"),sQuery(id+"F0.wireOp",EDGE,"E15.5.2"),sQuery(id+"F0.wireOp",EDGE,"E15.5.3"),sQuery(id+"F0.wireOp",EDGE,"E15.6.0"),sQuery(id+"F0.wireOp",EDGE,"E15.6.1"),sQuery(id+"F0.wireOp",EDGE,"E15.6.2"),sQuery(id+"F0.wireOp",EDGE,"E15.6.3"),sQuery(id+"F0.wireOp",EDGE,"E15.7.0"),sQuery(id+"F0.wireOp",EDGE,"E15.7.1"),sQuery(id+"F0.wireOp",EDGE,"E15.7.2"),sQuery(id+"F0.wireOp",EDGE,"E15.7.3"),sQuery(id+"F0.wireOp",EDGE,"E15.8.0"),sQuery(id+"F0.wireOp",EDGE,"E15.8.1"),sQuery(id+"F0.wireOp",EDGE,"E15.8.2"),sQuery(id+"F0.wireOp",EDGE,"E15.8.3"),sQuery(id+"F0.wireOp",EDGE,"E15.9.0"),sQuery(id+"F0.wireOp",EDGE,"E15.9.1"),sQuery(id+"F0.wireOp",EDGE,"E15.9.2"),sQuery(id+"F0.wireOp",EDGE,"E15.9.3"),sQuery(id+"F0.wireOp",EDGE,"E15.10.0"),sQuery(id+"F0.wireOp",EDGE,"E15.10.1"),sQuery(id+"F0.wireOp",EDGE,"E15.10.2"),sQuery(id+"F0.wireOp",EDGE,"E15.10.3"),sQuery(id+"F0.wireOp",EDGE,"E15.11.0"),sQuery(id+"F0.wireOp",EDGE,"E15.11.1"),sQuery(id+"F0.wireOp",EDGE,"E15.11.2"),sQuery(id+"F0.wireOp",EDGE,"E15.11.3"),sQuery(id+"F0.wireOp",EDGE,"E16.bottom"),sQuery(id+"F0.wireOp",EDGE,"E16.top"),sQuery(id+"F0.wireOp",EDGE,"E16.left"),sQuery(id+"F0.wireOp",EDGE,"E16.right")])],"isStart":false}),makeQuery(id+"F6.opExtrude","CAP_FACE",FACE,{"disambiguationData":[OSD([sQuery(id+"F5.wireOp",EDGE,"E18"),sQuery(id+"F5.wireOp",EDGE,"E19")])],"isStart":true})]});
            var sketch = newSketch(context, id + "F9", { "sketchPlane" : qUnion([Q0])});
            skCircle(sketch, "E21", {"center": v(0, 0) * mm, "radius": 17.5 * mm});
            skCircle(sketch, "E22", {"center": v(0, 0) * mm, "radius": 11 * mm});
            skSolve(sketch);
        }
        {
            var Q0;
            Q0 = qSketchRegion(id + "F9", true);
            extrude(context, id + "F10", {"entities" : qUnion([Q0]), "oppositeDirection" : true, "depth" : 5 * mm, "offsetDistance" : 25 * mm});
        }
    });
